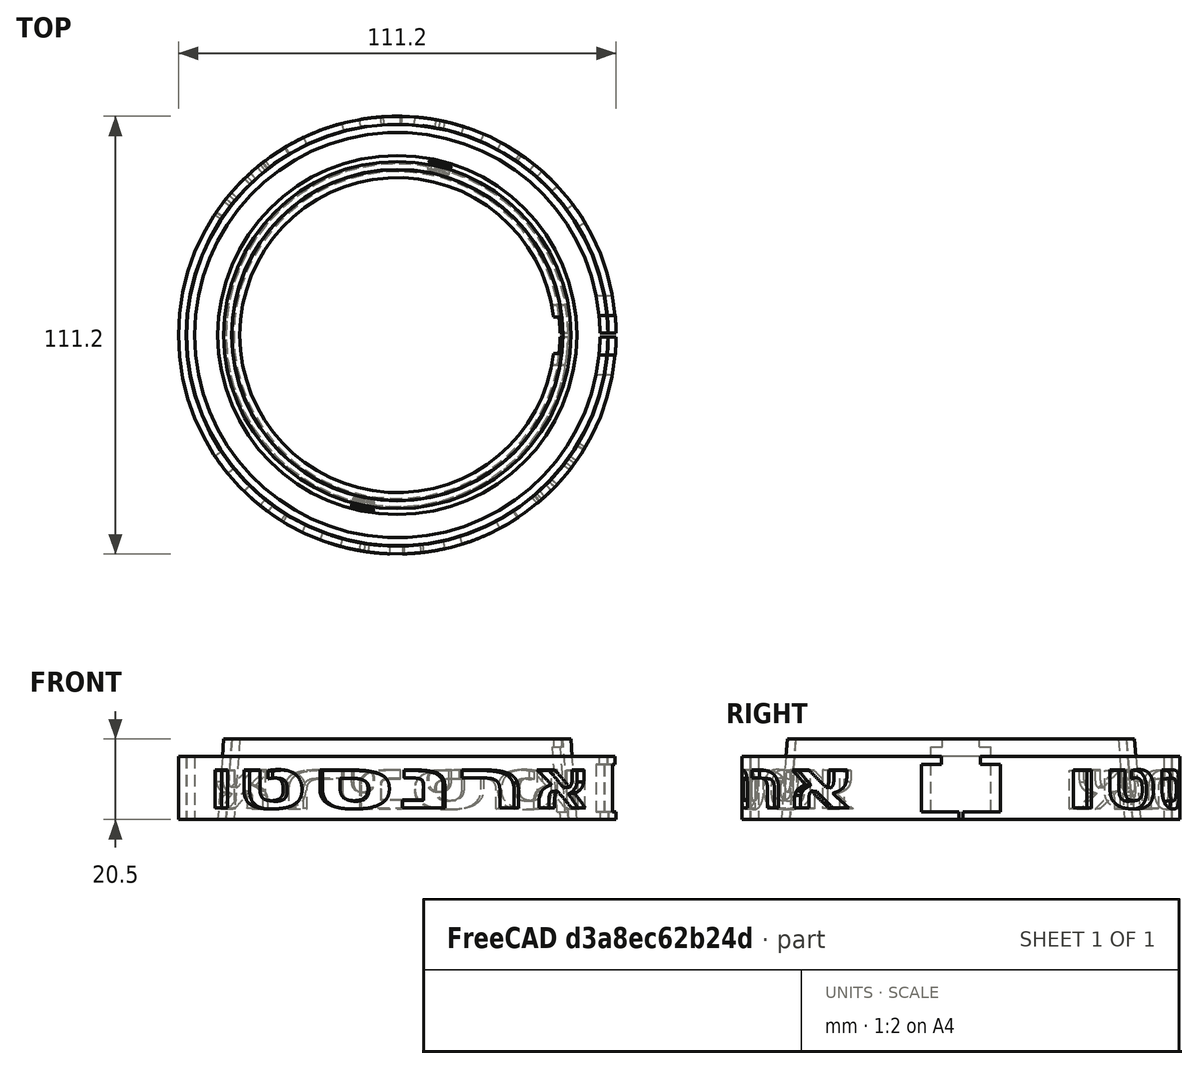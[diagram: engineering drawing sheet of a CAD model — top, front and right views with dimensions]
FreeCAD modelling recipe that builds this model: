
FCSTD DOCUMENT  (FreeCAD 0.20R29603 (Git))
Label: tazas
License: All rights reserved
LicenseURL: http://en.wikipedia.org/wiki/All_rights_reserved
objects: Part::Box×12, Part::Cut×11, Part::Feature×7, App::DocumentObjectGroup×7, Part::Cone×6, Sketcher::SketchObject×5, Part::Cylinder×4, Part::MultiFuse×4, Mesh::Feature×4, Part::FeaturePython×3
note: 52 computed .brp shape members not serialized (recipe doc carries the construction recipe); baked Part::Feature solids carry a one-line shape summary decoded from their .brp

FEATURE [Part::Cylinder] Cylinder  label="Cylinder_chico"
  Angle = 360
  AttacherType = Attacher::AttachEngine3D
  FirstAngle = 0
  Height = 16
  Radius = 51.5
  SecondAngle = 0
FEATURE [Part::Cylinder] Cylinder001  label="Cylinder00_grande"
  Angle = 360
  AttacherType = Attacher::AttachEngine3D
  FirstAngle = 0
  Height = 16
  Radius = 53.5
  SecondAngle = 0
FEATURE [Part::Cone] Cone  label="Cone_chico"
  Angle = 360
  AttacherType = Attacher::AttachEngine3D
  Height = 20.5
  Radius1 = 41.5
  Radius2 = 40
FEATURE [Part::Cone] Cone001  label="Cone001_grande"
  Angle = 360
  AttacherType = Attacher::AttachEngine3D
  Height = 20.5
  Radius1 = 43.5
  Radius2 = 42
FEATURE [Part::Box] Box  label="Cube"
  AttacherType = Attacher::AttachEngine3D
  Height = 12
  Length = 25
  Placement = pos=(40,-10,2) rot=(0,0,1;0rad)
  Width = 20
FEATURE [Part::Box] Box002  label="Cube002"
  AttacherType = Attacher::AttachEngine3D
  Height = 25.45
  Length = 25
  Placement = pos=(40,-5,2.55) rot=(0,0,1;0rad)
  Width = 10
FEATURE [Part::Box] Box003  label="Cube003"
  AttacherType = Attacher::AttachEngine3D
  Height = 12
  Length = 25
  Placement = pos=(40,-10,2) rot=(0,0,1;0rad)
  Width = 20
FEATURE [Part::Box] Box004  label="Cube004"
  AttacherType = Attacher::AttachEngine3D
  Height = 25.45
  Length = 25
  Placement = pos=(40,-5,4) rot=(0,0,1;0rad)
  Width = 10
FEATURE [Part::Cylinder] Cylinder002  label="Cylinder002_chico"
  Angle = 360
  AttacherType = Attacher::AttachEngine3D
  FirstAngle = 0
  Height = 16
  Radius = 53.6
  SecondAngle = 0
FEATURE [Part::Cylinder] Cylinder003  label="Cylinder003-grande"
  Angle = 360
  AttacherType = Attacher::AttachEngine3D
  FirstAngle = 0
  Height = 16
  Radius = 55.6
  SecondAngle = 0
FEATURE [Part::Box] Box006  label="Cube006"
  AttacherType = Attacher::AttachEngine3D
  Height = 16.5
  Length = 30
  Placement = pos=(24,-7.65,2) rot=(0,0,1;0rad)
  Width = 15.3
FEATURE [Part::Box] Box007  label="Cube007"
  AttacherType = Attacher::AttachEngine3D
  Height = 25.5
  Length = 30
  Placement = pos=(24,-4.65,2) rot=(0,0,1;0rad)
  Width = 9.3
FEATURE [Part::Cone] Cone002  label="Cone_chico001"
  Angle = 360
  AttacherType = Attacher::AttachEngine3D
  Height = 20.5
  Radius1 = 43.6
  Radius2 = 42.1
FEATURE [Part::Cone] Cone003  label="Cone001_grande001"
  Angle = 360
  AttacherType = Attacher::AttachEngine3D
  Height = 20.5
  Radius1 = 45.6
  Radius2 = 44.1
FEATURE [Part::Feature] Face003
  shape: bbox 14.35 x 9.888 x 2.467e-07 mm, 1 faces, 0 solids (baked)
FEATURE [Part::Feature] Face004
  shape: bbox 5.698 x 5.643 x 2.467e-07 mm, 1 faces, 0 solids (baked)
FEATURE [Part::Feature] Compound
  Placement = pos=(69.91,10.15,0) rot=(0,0,1;0rad)
  shape: bbox 89.01 x 10 x 2.467e-07 mm, 6 faces, 0 solids (baked)
FEATURE [Part::Feature] Compound001
  Placement = pos=(189.91,10.15,0) rot=(0,0,1;0rad)
  shape: bbox 89.01 x 10 x 2.467e-07 mm, 6 faces, 0 solids (baked)
FEATURE [Part::Feature] Compound004  label="2_ernesto"
  Placement = pos=(-33.35,18,0) rot=(1,0,0;0rad)
  shape: bbox 229.5 x 10 x 2.467e-07 mm, 12 faces, 0 solids (baked)
FEATURE [Part::Cut] Cut015014  label="taza_interior"
  Base = -> Cone001
  Tool = -> Cone
FEATURE [Part::Cut] Cut015018  label="cono"
  Base = -> Cone003
  Tool = -> Cone002
FEATURE [Part::Box] Box009  label="Cube009"
  AttacherType = Attacher::AttachEngine3D
  Height = 25.5
  Length = 30
  Placement = pos=(24,-0.5,-2) rot=(0,0,1;0rad)
  Width = 1
FEATURE [Part::Feature] Compound005  label="2_ernesto001"
  Placement = pos=(2.55,-16,0) rot=(1,0,0;3.14159rad)
  shape: bbox 229.5 x 10 x 2.467e-07 mm, 12 faces, 0 solids (baked)
FEATURE [Sketcher::SketchObject] Sketch  label="Sketch_con_2_ernesto"
  FullyConstrained = false
  sketch-geometry (180):
    g0: BSplineCurve PolesCount=2 KnotsCount=2 Degree=1 IsPeriodic=0
    g1: BSplineCurve PolesCount=3 KnotsCount=2 Degree=2 IsPeriodic=0
    g2: BSplineCurve PolesCount=3 KnotsCount=2 Degree=2 IsPeriodic=0
    g3: BSplineCurve PolesCount=3 KnotsCount=2 Degree=2 IsPeriodic=0
    g4: BSplineCurve PolesCount=3 KnotsCount=2 Degree=2 IsPeriodic=0
    g5: BSplineCurve PolesCount=3 KnotsCount=2 Degree=2 IsPeriodic=0
    g6: BSplineCurve PolesCount=3 KnotsCount=2 Degree=2 IsPeriodic=0
    g7: BSplineCurve PolesCount=2 KnotsCount=2 Degree=1 IsPeriodic=0
    g8: BSplineCurve PolesCount=3 KnotsCount=2 Degree=2 IsPeriodic=0
    g9: BSplineCurve PolesCount=2 KnotsCount=2 Degree=1 IsPeriodic=0
    g10: BSplineCurve PolesCount=2 KnotsCount=2 Degree=1 IsPeriodic=0
    g11: BSplineCurve PolesCount=3 KnotsCount=2 Degree=2 IsPeriodic=0
    g12: BSplineCurve PolesCount=3 KnotsCount=2 Degree=2 IsPeriodic=0
    g13: BSplineCurve PolesCount=3 KnotsCount=2 Degree=2 IsPeriodic=0
    g14: BSplineCurve PolesCount=3 KnotsCount=2 Degree=2 IsPeriodic=0
    g15: BSplineCurve PolesCount=3 KnotsCount=2 Degree=2 IsPeriodic=0
    g16: BSplineCurve PolesCount=2 KnotsCount=2 Degree=1 IsPeriodic=0
    g17: BSplineCurve PolesCount=2 KnotsCount=2 Degree=1 IsPeriodic=0
    g18: BSplineCurve PolesCount=2 KnotsCount=2 Degree=1 IsPeriodic=0
    g19: BSplineCurve PolesCount=3 KnotsCount=2 Degree=2 IsPeriodic=0
    g20: BSplineCurve PolesCount=2 KnotsCount=2 Degree=1 IsPeriodic=0
    g21: BSplineCurve PolesCount=2 KnotsCount=2 Degree=1 IsPeriodic=0
    g22: BSplineCurve PolesCount=2 KnotsCount=2 Degree=1 IsPeriodic=0
    g23: BSplineCurve PolesCount=3 KnotsCount=2 Degree=2 IsPeriodic=0
    g24: BSplineCurve PolesCount=3 KnotsCount=2 Degree=2 IsPeriodic=0
    g25: BSplineCurve PolesCount=3 KnotsCount=2 Degree=2 IsPeriodic=0
    g26: BSplineCurve PolesCount=3 KnotsCount=2 Degree=2 IsPeriodic=0
    g27: BSplineCurve PolesCount=3 KnotsCount=2 Degree=2 IsPeriodic=0
    g28: BSplineCurve PolesCount=2 KnotsCount=2 Degree=1 IsPeriodic=0
    g29: BSplineCurve PolesCount=2 KnotsCount=2 Degree=1 IsPeriodic=0
    g30: BSplineCurve PolesCount=2 KnotsCount=2 Degree=1 IsPeriodic=0
    g31: BSplineCurve PolesCount=3 KnotsCount=2 Degree=2 IsPeriodic=0
    g32: BSplineCurve PolesCount=2 KnotsCount=2 Degree=1 IsPeriodic=0
    g33: BSplineCurve PolesCount=2 KnotsCount=2 Degree=1 IsPeriodic=0
    g34: BSplineCurve PolesCount=2 KnotsCount=2 Degree=1 IsPeriodic=0
    g35: BSplineCurve PolesCount=3 KnotsCount=2 Degree=2 IsPeriodic=0
    g36: BSplineCurve PolesCount=3 KnotsCount=2 Degree=2 IsPeriodic=0
    g37: BSplineCurve PolesCount=3 KnotsCount=2 Degree=2 IsPeriodic=0
    g38: BSplineCurve PolesCount=3 KnotsCount=2 Degree=2 IsPeriodic=0
    g39: BSplineCurve PolesCount=3 KnotsCount=2 Degree=2 IsPeriodic=0
    g40: BSplineCurve PolesCount=3 KnotsCount=2 Degree=2 IsPeriodic=0
    g41: BSplineCurve PolesCount=3 KnotsCount=2 Degree=2 IsPeriodic=0
    g42: BSplineCurve PolesCount=2 KnotsCount=2 Degree=1 IsPeriodic=0
    g43: BSplineCurve PolesCount=2 KnotsCount=2 Degree=1 IsPeriodic=0
    g44: BSplineCurve PolesCount=2 KnotsCount=2 Degree=1 IsPeriodic=0
    g45: BSplineCurve PolesCount=2 KnotsCount=2 Degree=1 IsPeriodic=0
    g46: BSplineCurve PolesCount=3 KnotsCount=2 Degree=2 IsPeriodic=0
    g47: BSplineCurve PolesCount=3 KnotsCount=2 Degree=2 IsPeriodic=0
    g48: BSplineCurve PolesCount=2 KnotsCount=2 Degree=1 IsPeriodic=0
    g49: BSplineCurve PolesCount=2 KnotsCount=2 Degree=1 IsPeriodic=0
    g50: BSplineCurve PolesCount=2 KnotsCount=2 Degree=1 IsPeriodic=0
    g51: BSplineCurve PolesCount=3 KnotsCount=2 Degree=2 IsPeriodic=0
    g52: BSplineCurve PolesCount=3 KnotsCount=2 Degree=2 IsPeriodic=0
    g53: BSplineCurve PolesCount=3 KnotsCount=2 Degree=2 IsPeriodic=0
    g54: BSplineCurve PolesCount=3 KnotsCount=2 Degree=2 IsPeriodic=0
    g55: BSplineCurve PolesCount=3 KnotsCount=2 Degree=2 IsPeriodic=0
    g56: BSplineCurve PolesCount=2 KnotsCount=2 Degree=1 IsPeriodic=0
    g57: BSplineCurve PolesCount=3 KnotsCount=2 Degree=2 IsPeriodic=0
    g58: BSplineCurve PolesCount=3 KnotsCount=2 Degree=2 IsPeriodic=0
    g59: BSplineCurve PolesCount=2 KnotsCount=2 Degree=1 IsPeriodic=0
    g60: BSplineCurve PolesCount=2 KnotsCount=2 Degree=1 IsPeriodic=0
    g61: BSplineCurve PolesCount=2 KnotsCount=2 Degree=1 IsPeriodic=0
    g62: BSplineCurve PolesCount=3 KnotsCount=2 Degree=2 IsPeriodic=0
    g63: BSplineCurve PolesCount=3 KnotsCount=2 Degree=2 IsPeriodic=0
    g64: BSplineCurve PolesCount=2 KnotsCount=2 Degree=1 IsPeriodic=0
    g65: BSplineCurve PolesCount=2 KnotsCount=2 Degree=1 IsPeriodic=0
    g66: BSplineCurve PolesCount=2 KnotsCount=2 Degree=1 IsPeriodic=0
    g67: BSplineCurve PolesCount=2 KnotsCount=2 Degree=1 IsPeriodic=0
    g68: BSplineCurve PolesCount=2 KnotsCount=2 Degree=1 IsPeriodic=0
    g69: BSplineCurve PolesCount=3 KnotsCount=2 Degree=2 IsPeriodic=0
    g70: BSplineCurve PolesCount=3 KnotsCount=2 Degree=2 IsPeriodic=0
    g71: BSplineCurve PolesCount=3 KnotsCount=2 Degree=2 IsPeriodic=0
    g72: BSplineCurve PolesCount=3 KnotsCount=2 Degree=2 IsPeriodic=0
    g73: BSplineCurve PolesCount=3 KnotsCount=2 Degree=2 IsPeriodic=0
    g74: BSplineCurve PolesCount=3 KnotsCount=2 Degree=2 IsPeriodic=0
    g75: BSplineCurve PolesCount=3 KnotsCount=2 Degree=2 IsPeriodic=0
    g76: BSplineCurve PolesCount=2 KnotsCount=2 Degree=1 IsPeriodic=0
    g77: BSplineCurve PolesCount=3 KnotsCount=2 Degree=2 IsPeriodic=0
    g78: BSplineCurve PolesCount=3 KnotsCount=2 Degree=2 IsPeriodic=0
    g79: BSplineCurve PolesCount=3 KnotsCount=2 Degree=2 IsPeriodic=0
    g80: BSplineCurve PolesCount=3 KnotsCount=2 Degree=2 IsPeriodic=0
    g81: BSplineCurve PolesCount=3 KnotsCount=2 Degree=2 IsPeriodic=0
    g82: BSplineCurve PolesCount=3 KnotsCount=2 Degree=2 IsPeriodic=0
    g83: BSplineCurve PolesCount=3 KnotsCount=2 Degree=2 IsPeriodic=0
    g84: BSplineCurve PolesCount=2 KnotsCount=2 Degree=1 IsPeriodic=0
    g85: BSplineCurve PolesCount=2 KnotsCount=2 Degree=1 IsPeriodic=0
    g86: BSplineCurve PolesCount=2 KnotsCount=2 Degree=1 IsPeriodic=0
    g87: BSplineCurve PolesCount=2 KnotsCount=2 Degree=1 IsPeriodic=0
    g88: BSplineCurve PolesCount=2 KnotsCount=2 Degree=1 IsPeriodic=0
    g89: BSplineCurve PolesCount=2 KnotsCount=2 Degree=1 IsPeriodic=0
    g90: BSplineCurve PolesCount=2 KnotsCount=2 Degree=1 IsPeriodic=0
    g91: BSplineCurve PolesCount=3 KnotsCount=2 Degree=2 IsPeriodic=0
    g92: BSplineCurve PolesCount=3 KnotsCount=2 Degree=2 IsPeriodic=0
    g93: BSplineCurve PolesCount=3 KnotsCount=2 Degree=2 IsPeriodic=0
    g94: BSplineCurve PolesCount=3 KnotsCount=2 Degree=2 IsPeriodic=0
    g95: BSplineCurve PolesCount=3 KnotsCount=2 Degree=2 IsPeriodic=0
    g96: BSplineCurve PolesCount=3 KnotsCount=2 Degree=2 IsPeriodic=0
    g97: BSplineCurve PolesCount=2 KnotsCount=2 Degree=1 IsPeriodic=0
    g98: BSplineCurve PolesCount=3 KnotsCount=2 Degree=2 IsPeriodic=0
    g99: BSplineCurve PolesCount=2 KnotsCount=2 Degree=1 IsPeriodic=0
    g100: BSplineCurve PolesCount=2 KnotsCount=2 Degree=1 IsPeriodic=0
    g101: BSplineCurve PolesCount=3 KnotsCount=2 Degree=2 IsPeriodic=0
    g102: BSplineCurve PolesCount=3 KnotsCount=2 Degree=2 IsPeriodic=0
    g103: BSplineCurve PolesCount=3 KnotsCount=2 Degree=2 IsPeriodic=0
    g104: BSplineCurve PolesCount=3 KnotsCount=2 Degree=2 IsPeriodic=0
    g105: BSplineCurve PolesCount=3 KnotsCount=2 Degree=2 IsPeriodic=0
    g106: BSplineCurve PolesCount=2 KnotsCount=2 Degree=1 IsPeriodic=0
    g107: BSplineCurve PolesCount=2 KnotsCount=2 Degree=1 IsPeriodic=0
    g108: BSplineCurve PolesCount=2 KnotsCount=2 Degree=1 IsPeriodic=0
    g109: BSplineCurve PolesCount=3 KnotsCount=2 Degree=2 IsPeriodic=0
    g110: BSplineCurve PolesCount=2 KnotsCount=2 Degree=1 IsPeriodic=0
    g111: BSplineCurve PolesCount=2 KnotsCount=2 Degree=1 IsPeriodic=0
    g112: BSplineCurve PolesCount=2 KnotsCount=2 Degree=1 IsPeriodic=0
    g113: BSplineCurve PolesCount=3 KnotsCount=2 Degree=2 IsPeriodic=0
    g114: BSplineCurve PolesCount=3 KnotsCount=2 Degree=2 IsPeriodic=0
    g115: BSplineCurve PolesCount=3 KnotsCount=2 Degree=2 IsPeriodic=0
    g116: BSplineCurve PolesCount=3 KnotsCount=2 Degree=2 IsPeriodic=0
    g117: BSplineCurve PolesCount=3 KnotsCount=2 Degree=2 IsPeriodic=0
    g118: BSplineCurve PolesCount=2 KnotsCount=2 Degree=1 IsPeriodic=0
    g119: BSplineCurve PolesCount=2 KnotsCount=2 Degree=1 IsPeriodic=0
    g120: BSplineCurve PolesCount=2 KnotsCount=2 Degree=1 IsPeriodic=0
    g121: BSplineCurve PolesCount=3 KnotsCount=2 Degree=2 IsPeriodic=0
    g122: BSplineCurve PolesCount=2 KnotsCount=2 Degree=1 IsPeriodic=0
    g123: BSplineCurve PolesCount=2 KnotsCount=2 Degree=1 IsPeriodic=0
    g124: BSplineCurve PolesCount=2 KnotsCount=2 Degree=1 IsPeriodic=0
    g125: BSplineCurve PolesCount=3 KnotsCount=2 Degree=2 IsPeriodic=0
    g126: BSplineCurve PolesCount=3 KnotsCount=2 Degree=2 IsPeriodic=0
    g127: BSplineCurve PolesCount=3 KnotsCount=2 Degree=2 IsPeriodic=0
    g128: BSplineCurve PolesCount=3 KnotsCount=2 Degree=2 IsPeriodic=0
    g129: BSplineCurve PolesCount=3 KnotsCount=2 Degree=2 IsPeriodic=0
    g130: BSplineCurve PolesCount=3 KnotsCount=2 Degree=2 IsPeriodic=0
    g131: BSplineCurve PolesCount=3 KnotsCount=2 Degree=2 IsPeriodic=0
    g132: BSplineCurve PolesCount=2 KnotsCount=2 Degree=1 IsPeriodic=0
    g133: BSplineCurve PolesCount=2 KnotsCount=2 Degree=1 IsPeriodic=0
    g134: BSplineCurve PolesCount=2 KnotsCount=2 Degree=1 IsPeriodic=0
    g135: BSplineCurve PolesCount=2 KnotsCount=2 Degree=1 IsPeriodic=0
    g136: BSplineCurve PolesCount=3 KnotsCount=2 Degree=2 IsPeriodic=0
    g137: BSplineCurve PolesCount=3 KnotsCount=2 Degree=2 IsPeriodic=0
    g138: BSplineCurve PolesCount=2 KnotsCount=2 Degree=1 IsPeriodic=0
    g139: BSplineCurve PolesCount=2 KnotsCount=2 Degree=1 IsPeriodic=0
    g140: BSplineCurve PolesCount=2 KnotsCount=2 Degree=1 IsPeriodic=0
    g141: BSplineCurve PolesCount=3 KnotsCount=2 Degree=2 IsPeriodic=0
    g142: BSplineCurve PolesCount=3 KnotsCount=2 Degree=2 IsPeriodic=0
    g143: BSplineCurve PolesCount=3 KnotsCount=2 Degree=2 IsPeriodic=0
    g144: BSplineCurve PolesCount=3 KnotsCount=2 Degree=2 IsPeriodic=0
    g145: BSplineCurve PolesCount=3 KnotsCount=2 Degree=2 IsPeriodic=0
    g146: BSplineCurve PolesCount=2 KnotsCount=2 Degree=1 IsPeriodic=0
    g147: BSplineCurve PolesCount=3 KnotsCount=2 Degree=2 IsPeriodic=0
    g148: BSplineCurve PolesCount=3 KnotsCount=2 Degree=2 IsPeriodic=0
    g149: BSplineCurve PolesCount=2 KnotsCount=2 Degree=1 IsPeriodic=0
    g150: BSplineCurve PolesCount=2 KnotsCount=2 Degree=1 IsPeriodic=0
    g151: BSplineCurve PolesCount=2 KnotsCount=2 Degree=1 IsPeriodic=0
    g152: BSplineCurve PolesCount=3 KnotsCount=2 Degree=2 IsPeriodic=0
    g153: BSplineCurve PolesCount=3 KnotsCount=2 Degree=2 IsPeriodic=0
    g154: BSplineCurve PolesCount=2 KnotsCount=2 Degree=1 IsPeriodic=0
    g155: BSplineCurve PolesCount=2 KnotsCount=2 Degree=1 IsPeriodic=0
    g156: BSplineCurve PolesCount=2 KnotsCount=2 Degree=1 IsPeriodic=0
    g157: BSplineCurve PolesCount=2 KnotsCount=2 Degree=1 IsPeriodic=0
    g158: BSplineCurve PolesCount=2 KnotsCount=2 Degree=1 IsPeriodic=0
    g159: BSplineCurve PolesCount=3 KnotsCount=2 Degree=2 IsPeriodic=0
    g160: BSplineCurve PolesCount=3 KnotsCount=2 Degree=2 IsPeriodic=0
    g161: BSplineCurve PolesCount=3 KnotsCount=2 Degree=2 IsPeriodic=0
    g162: BSplineCurve PolesCount=3 KnotsCount=2 Degree=2 IsPeriodic=0
    g163: BSplineCurve PolesCount=3 KnotsCount=2 Degree=2 IsPeriodic=0
    g164: BSplineCurve PolesCount=3 KnotsCount=2 Degree=2 IsPeriodic=0
    g165: BSplineCurve PolesCount=3 KnotsCount=2 Degree=2 IsPeriodic=0
    g166: BSplineCurve PolesCount=2 KnotsCount=2 Degree=1 IsPeriodic=0
    g167: BSplineCurve PolesCount=3 KnotsCount=2 Degree=2 IsPeriodic=0
    g168: BSplineCurve PolesCount=3 KnotsCount=2 Degree=2 IsPeriodic=0
    g169: BSplineCurve PolesCount=3 KnotsCount=2 Degree=2 IsPeriodic=0
    g170: BSplineCurve PolesCount=3 KnotsCount=2 Degree=2 IsPeriodic=0
    g171: BSplineCurve PolesCount=3 KnotsCount=2 Degree=2 IsPeriodic=0
    g172: BSplineCurve PolesCount=3 KnotsCount=2 Degree=2 IsPeriodic=0
    g173: BSplineCurve PolesCount=3 KnotsCount=2 Degree=2 IsPeriodic=0
    g174: BSplineCurve PolesCount=2 KnotsCount=2 Degree=1 IsPeriodic=0
    g175: BSplineCurve PolesCount=2 KnotsCount=2 Degree=1 IsPeriodic=0
    g176: BSplineCurve PolesCount=2 KnotsCount=2 Degree=1 IsPeriodic=0
    g177: BSplineCurve PolesCount=2 KnotsCount=2 Degree=1 IsPeriodic=0
    g178: BSplineCurve PolesCount=2 KnotsCount=2 Degree=1 IsPeriodic=0
    g179: BSplineCurve PolesCount=2 KnotsCount=2 Degree=1 IsPeriodic=0
  constraints (180):
    c: Coincident(g0,g1)
    c: Coincident(g1,g2)
    c: Coincident(g2,g3)
    c: Coincident(g3,g4)
    c: Coincident(g4,g5)
    c: Coincident(g5,g6)
    c: Coincident(g6,g7)
    c: Coincident(g7,g0)
    c: Coincident(g8,g9)
    c: Coincident(g9,g10)
    c: Coincident(g10,g11)
    c: Coincident(g11,g12)
    c: Coincident(g12,g13)
    c: Coincident(g13,g14)
    c: Coincident(g14,g15)
    c: Coincident(g15,g8)
    c: Coincident(g16,g17)
    c: Coincident(g17,g18)
    c: Coincident(g18,g19)
    c: Coincident(g19,g20)
    c: Coincident(g20,g21)
    c: Coincident(g21,g22)
    c: Coincident(g22,g23)
    c: Coincident(g23,g24)
    c: Coincident(g24,g25)
    c: Coincident(g25,g26)
    c: Coincident(g26,g27)
    c: Coincident(g27,g28)
    c: Coincident(g28,g29)
    c: Coincident(g29,g30)
    c: Coincident(g30,g31)
    c: Coincident(g31,g32)
    c: Coincident(g32,g33)
    c: Coincident(g33,g34)
    c: Coincident(g34,g35)
    c: Coincident(g35,g36)
    c: Coincident(g36,g37)
    c: Coincident(g37,g38)
    c: Coincident(g38,g39)
    c: Coincident(g39,g40)
    c: Coincident(g40,g41)
    c: Coincident(g41,g42)
    c: Coincident(g42,g16)
    c: Coincident(g43,g44)
    c: Coincident(g44,g45)
    c: Coincident(g45,g46)
    c: Coincident(g46,g47)
    c: Coincident(g47,g48)
    c: Coincident(g48,g49)
    c: Coincident(g49,g50)
    c: Coincident(g50,g51)
    c: Coincident(g51,g52)
    c: Coincident(g52,g53)
    c: Coincident(g53,g54)
    c: Coincident(g54,g55)
    c: Coincident(g55,g43)
    c: Coincident(g56,g57)
    c: Coincident(g57,g58)
    c: Coincident(g58,g59)
    c: Coincident(g59,g60)
    c: Coincident(g60,g61)
    c: Coincident(g61,g62)
    c: Coincident(g62,g63)
    c: Coincident(g63,g64)
    c: Coincident(g64,g65)
    c: Coincident(g65,g66)
    c: Coincident(g66,g67)
    c: Coincident(g67,g56)
    c: Coincident(g68,g69)
    c: Coincident(g69,g70)
    c: Coincident(g70,g71)
    c: Coincident(g71,g72)
    c: Coincident(g72,g73)
    c: Coincident(g73,g74)
    c: Coincident(g74,g75)
    c: Coincident(g75,g76)
    c: Coincident(g76,g77)
    c: Coincident(g77,g78)
    c: Coincident(g78,g79)
    c: Coincident(g79,g80)
    c: Coincident(g80,g81)
    c: Coincident(g81,g82)
    c: Coincident(g82,g83)
    c: Coincident(g83,g84)
    c: Coincident(g84,g85)
    c: Coincident(g85,g68)
    c: Coincident(g86,g87)
    c: Coincident(g87,g88)
    c: Coincident(g88,g89)
    c: Coincident(g89,g86)
    c: Coincident(g90,g91)
    c: Coincident(g91,g92)
    c: Coincident(g92,g93)
    c: Coincident(g93,g94)
    c: Coincident(g94,g95)
    c: Coincident(g95,g96)
    c: Coincident(g96,g97)
    c: Coincident(g97,g90)
    c: Coincident(g98,g99)
    c: Coincident(g99,g100)
    c: Coincident(g100,g101)
    c: Coincident(g101,g102)
    c: Coincident(g102,g103)
    c: Coincident(g103,g104)
    c: Coincident(g104,g105)
    c: Coincident(g105,g98)
    c: Coincident(g106,g107)
    c: Coincident(g107,g108)
    c: Coincident(g108,g109)
    c: Coincident(g109,g110)
    c: Coincident(g110,g111)
    c: Coincident(g111,g112)
    c: Coincident(g112,g113)
    c: Coincident(g113,g114)
    c: Coincident(g114,g115)
    c: Coincident(g115,g116)
    c: Coincident(g116,g117)
    c: Coincident(g117,g118)
    c: Coincident(g118,g119)
    c: Coincident(g119,g120)
    c: Coincident(g120,g121)
    c: Coincident(g121,g122)
    c: Coincident(g122,g123)
    c: Coincident(g123,g124)
    c: Coincident(g124,g125)
    c: Coincident(g125,g126)
    c: Coincident(g126,g127)
    c: Coincident(g127,g128)
    c: Coincident(g128,g129)
    c: Coincident(g129,g130)
    c: Coincident(g130,g131)
    c: Coincident(g131,g132)
    c: Coincident(g132,g106)
    c: Coincident(g133,g134)
    c: Coincident(g134,g135)
    c: Coincident(g135,g136)
    c: Coincident(g136,g137)
    c: Coincident(g137,g138)
    c: Coincident(g138,g139)
    c: Coincident(g139,g140)
    c: Coincident(g140,g141)
    c: Coincident(g141,g142)
    c: Coincident(g142,g143)
    c: Coincident(g143,g144)
    c: Coincident(g144,g145)
    c: Coincident(g145,g133)
    c: Coincident(g146,g147)
    c: Coincident(g147,g148)
    c: Coincident(g148,g149)
    c: Coincident(g149,g150)
    c: Coincident(g150,g151)
    c: Coincident(g151,g152)
    c: Coincident(g152,g153)
    c: Coincident(g153,g154)
    c: Coincident(g154,g155)
    c: Coincident(g155,g156)
    c: Coincident(g156,g157)
    c: Coincident(g157,g146)
    c: Coincident(g158,g159)
    c: Coincident(g159,g160)
    c: Coincident(g160,g161)
    c: Coincident(g161,g162)
    c: Coincident(g162,g163)
    c: Coincident(g163,g164)
    c: Coincident(g164,g165)
    c: Coincident(g165,g166)
    c: Coincident(g166,g167)
    c: Coincident(g167,g168)
    c: Coincident(g168,g169)
    c: Coincident(g169,g170)
    c: Coincident(g170,g171)
    c: Coincident(g171,g172)
    c: Coincident(g172,g173)
    c: Coincident(g173,g174)
    c: Coincident(g174,g175)
    c: Coincident(g175,g158)
    c: Coincident(g176,g177)
    c: Coincident(g177,g178)
    c: Coincident(g178,g179)
    c: Coincident(g179,g176)
FEATURE [Sketcher::SketchObject] Mapped_Sketch
  FullyConstrained = false
  Support = -> [Cut015018]
  sketch-geometry (184):
    g0: LineSegment StartX=0 StartY=0 StartZ=0 EndX=277 EndY=0 EndZ=0
    g1: LineSegment StartX=277 StartY=0 StartZ=0 EndX=277 EndY=20.5548 EndZ=0
    g2: LineSegment StartX=277 StartY=20.5548 StartZ=0 EndX=0 EndY=20.5548 EndZ=0
    g3: LineSegment StartX=0 StartY=20.5548 StartZ=0 EndX=0 EndY=0 EndZ=0
    g4: BSplineCurve PolesCount=2 KnotsCount=2 Degree=1 IsPeriodic=0
    g5: BSplineCurve PolesCount=3 KnotsCount=2 Degree=2 IsPeriodic=0
    g6: BSplineCurve PolesCount=3 KnotsCount=2 Degree=2 IsPeriodic=0
    g7: BSplineCurve PolesCount=3 KnotsCount=2 Degree=2 IsPeriodic=0
    g8: BSplineCurve PolesCount=3 KnotsCount=2 Degree=2 IsPeriodic=0
    g9: BSplineCurve PolesCount=3 KnotsCount=2 Degree=2 IsPeriodic=0
    g10: BSplineCurve PolesCount=3 KnotsCount=2 Degree=2 IsPeriodic=0
    g11: BSplineCurve PolesCount=2 KnotsCount=2 Degree=1 IsPeriodic=0
    g12: BSplineCurve PolesCount=3 KnotsCount=2 Degree=2 IsPeriodic=0
    g13: BSplineCurve PolesCount=2 KnotsCount=2 Degree=1 IsPeriodic=0
    g14: BSplineCurve PolesCount=2 KnotsCount=2 Degree=1 IsPeriodic=0
    g15: BSplineCurve PolesCount=3 KnotsCount=2 Degree=2 IsPeriodic=0
    g16: BSplineCurve PolesCount=3 KnotsCount=2 Degree=2 IsPeriodic=0
    g17: BSplineCurve PolesCount=3 KnotsCount=2 Degree=2 IsPeriodic=0
    g18: BSplineCurve PolesCount=3 KnotsCount=2 Degree=2 IsPeriodic=0
    g19: BSplineCurve PolesCount=3 KnotsCount=2 Degree=2 IsPeriodic=0
    g20: BSplineCurve PolesCount=2 KnotsCount=2 Degree=1 IsPeriodic=0
    g21: BSplineCurve PolesCount=2 KnotsCount=2 Degree=1 IsPeriodic=0
    g22: BSplineCurve PolesCount=2 KnotsCount=2 Degree=1 IsPeriodic=0
    g23: BSplineCurve PolesCount=3 KnotsCount=2 Degree=2 IsPeriodic=0
    g24: BSplineCurve PolesCount=2 KnotsCount=2 Degree=1 IsPeriodic=0
    g25: BSplineCurve PolesCount=2 KnotsCount=2 Degree=1 IsPeriodic=0
    g26: BSplineCurve PolesCount=2 KnotsCount=2 Degree=1 IsPeriodic=0
    g27: BSplineCurve PolesCount=3 KnotsCount=2 Degree=2 IsPeriodic=0
    g28: BSplineCurve PolesCount=3 KnotsCount=2 Degree=2 IsPeriodic=0
    g29: BSplineCurve PolesCount=3 KnotsCount=2 Degree=2 IsPeriodic=0
    g30: BSplineCurve PolesCount=3 KnotsCount=2 Degree=2 IsPeriodic=0
    g31: BSplineCurve PolesCount=3 KnotsCount=2 Degree=2 IsPeriodic=0
    g32: BSplineCurve PolesCount=2 KnotsCount=2 Degree=1 IsPeriodic=0
    g33: BSplineCurve PolesCount=2 KnotsCount=2 Degree=1 IsPeriodic=0
    g34: BSplineCurve PolesCount=2 KnotsCount=2 Degree=1 IsPeriodic=0
    g35: BSplineCurve PolesCount=3 KnotsCount=2 Degree=2 IsPeriodic=0
    g36: BSplineCurve PolesCount=2 KnotsCount=2 Degree=1 IsPeriodic=0
    g37: BSplineCurve PolesCount=2 KnotsCount=2 Degree=1 IsPeriodic=0
    g38: BSplineCurve PolesCount=2 KnotsCount=2 Degree=1 IsPeriodic=0
    g39: BSplineCurve PolesCount=3 KnotsCount=2 Degree=2 IsPeriodic=0
    g40: BSplineCurve PolesCount=3 KnotsCount=2 Degree=2 IsPeriodic=0
    g41: BSplineCurve PolesCount=3 KnotsCount=2 Degree=2 IsPeriodic=0
    g42: BSplineCurve PolesCount=3 KnotsCount=2 Degree=2 IsPeriodic=0
    g43: BSplineCurve PolesCount=3 KnotsCount=2 Degree=2 IsPeriodic=0
    g44: BSplineCurve PolesCount=3 KnotsCount=2 Degree=2 IsPeriodic=0
    g45: BSplineCurve PolesCount=3 KnotsCount=2 Degree=2 IsPeriodic=0
    g46: BSplineCurve PolesCount=2 KnotsCount=2 Degree=1 IsPeriodic=0
    g47: BSplineCurve PolesCount=2 KnotsCount=2 Degree=1 IsPeriodic=0
    g48: BSplineCurve PolesCount=2 KnotsCount=2 Degree=1 IsPeriodic=0
    g49: BSplineCurve PolesCount=2 KnotsCount=2 Degree=1 IsPeriodic=0
    g50: BSplineCurve PolesCount=3 KnotsCount=2 Degree=2 IsPeriodic=0
    g51: BSplineCurve PolesCount=3 KnotsCount=2 Degree=2 IsPeriodic=0
    g52: BSplineCurve PolesCount=2 KnotsCount=2 Degree=1 IsPeriodic=0
    g53: BSplineCurve PolesCount=2 KnotsCount=2 Degree=1 IsPeriodic=0
    g54: BSplineCurve PolesCount=2 KnotsCount=2 Degree=1 IsPeriodic=0
    g55: BSplineCurve PolesCount=3 KnotsCount=2 Degree=2 IsPeriodic=0
    g56: BSplineCurve PolesCount=3 KnotsCount=2 Degree=2 IsPeriodic=0
    g57: BSplineCurve PolesCount=3 KnotsCount=2 Degree=2 IsPeriodic=0
    g58: BSplineCurve PolesCount=3 KnotsCount=2 Degree=2 IsPeriodic=0
    g59: BSplineCurve PolesCount=3 KnotsCount=2 Degree=2 IsPeriodic=0
    g60: BSplineCurve PolesCount=2 KnotsCount=2 Degree=1 IsPeriodic=0
    g61: BSplineCurve PolesCount=3 KnotsCount=2 Degree=2 IsPeriodic=0
    g62: BSplineCurve PolesCount=3 KnotsCount=2 Degree=2 IsPeriodic=0
    g63: BSplineCurve PolesCount=2 KnotsCount=2 Degree=1 IsPeriodic=0
    g64: BSplineCurve PolesCount=2 KnotsCount=2 Degree=1 IsPeriodic=0
    g65: BSplineCurve PolesCount=2 KnotsCount=2 Degree=1 IsPeriodic=0
    g66: BSplineCurve PolesCount=3 KnotsCount=2 Degree=2 IsPeriodic=0
    g67: BSplineCurve PolesCount=3 KnotsCount=2 Degree=2 IsPeriodic=0
    g68: BSplineCurve PolesCount=2 KnotsCount=2 Degree=1 IsPeriodic=0
    g69: BSplineCurve PolesCount=2 KnotsCount=2 Degree=1 IsPeriodic=0
    g70: BSplineCurve PolesCount=2 KnotsCount=2 Degree=1 IsPeriodic=0
    g71: BSplineCurve PolesCount=2 KnotsCount=2 Degree=1 IsPeriodic=0
    g72: BSplineCurve PolesCount=2 KnotsCount=2 Degree=1 IsPeriodic=0
    g73: BSplineCurve PolesCount=3 KnotsCount=2 Degree=2 IsPeriodic=0
    g74: BSplineCurve PolesCount=3 KnotsCount=2 Degree=2 IsPeriodic=0
    g75: BSplineCurve PolesCount=3 KnotsCount=2 Degree=2 IsPeriodic=0
    g76: BSplineCurve PolesCount=3 KnotsCount=2 Degree=2 IsPeriodic=0
    g77: BSplineCurve PolesCount=3 KnotsCount=2 Degree=2 IsPeriodic=0
    g78: BSplineCurve PolesCount=3 KnotsCount=2 Degree=2 IsPeriodic=0
    g79: BSplineCurve PolesCount=3 KnotsCount=2 Degree=2 IsPeriodic=0
    g80: BSplineCurve PolesCount=2 KnotsCount=2 Degree=1 IsPeriodic=0
    g81: BSplineCurve PolesCount=3 KnotsCount=2 Degree=2 IsPeriodic=0
    g82: BSplineCurve PolesCount=3 KnotsCount=2 Degree=2 IsPeriodic=0
    g83: BSplineCurve PolesCount=3 KnotsCount=2 Degree=2 IsPeriodic=0
    g84: BSplineCurve PolesCount=3 KnotsCount=2 Degree=2 IsPeriodic=0
    g85: BSplineCurve PolesCount=3 KnotsCount=2 Degree=2 IsPeriodic=0
    g86: BSplineCurve PolesCount=3 KnotsCount=2 Degree=2 IsPeriodic=0
    g87: BSplineCurve PolesCount=3 KnotsCount=2 Degree=2 IsPeriodic=0
    g88: BSplineCurve PolesCount=2 KnotsCount=2 Degree=1 IsPeriodic=0
    g89: BSplineCurve PolesCount=2 KnotsCount=2 Degree=1 IsPeriodic=0
    g90: BSplineCurve PolesCount=2 KnotsCount=2 Degree=1 IsPeriodic=0
    g91: BSplineCurve PolesCount=2 KnotsCount=2 Degree=1 IsPeriodic=0
    g92: BSplineCurve PolesCount=2 KnotsCount=2 Degree=1 IsPeriodic=0
    g93: BSplineCurve PolesCount=2 KnotsCount=2 Degree=1 IsPeriodic=0
    g94: BSplineCurve PolesCount=2 KnotsCount=2 Degree=1 IsPeriodic=0
    g95: BSplineCurve PolesCount=3 KnotsCount=2 Degree=2 IsPeriodic=0
    g96: BSplineCurve PolesCount=3 KnotsCount=2 Degree=2 IsPeriodic=0
    g97: BSplineCurve PolesCount=3 KnotsCount=2 Degree=2 IsPeriodic=0
    g98: BSplineCurve PolesCount=3 KnotsCount=2 Degree=2 IsPeriodic=0
    g99: BSplineCurve PolesCount=3 KnotsCount=2 Degree=2 IsPeriodic=0
    g100: BSplineCurve PolesCount=3 KnotsCount=2 Degree=2 IsPeriodic=0
    g101: BSplineCurve PolesCount=2 KnotsCount=2 Degree=1 IsPeriodic=0
    g102: BSplineCurve PolesCount=3 KnotsCount=2 Degree=2 IsPeriodic=0
    g103: BSplineCurve PolesCount=2 KnotsCount=2 Degree=1 IsPeriodic=0
    g104: BSplineCurve PolesCount=2 KnotsCount=2 Degree=1 IsPeriodic=0
    g105: BSplineCurve PolesCount=3 KnotsCount=2 Degree=2 IsPeriodic=0
    g106: BSplineCurve PolesCount=3 KnotsCount=2 Degree=2 IsPeriodic=0
    g107: BSplineCurve PolesCount=3 KnotsCount=2 Degree=2 IsPeriodic=0
    g108: BSplineCurve PolesCount=3 KnotsCount=2 Degree=2 IsPeriodic=0
    g109: BSplineCurve PolesCount=3 KnotsCount=2 Degree=2 IsPeriodic=0
    g110: BSplineCurve PolesCount=2 KnotsCount=2 Degree=1 IsPeriodic=0
    g111: BSplineCurve PolesCount=2 KnotsCount=2 Degree=1 IsPeriodic=0
    g112: BSplineCurve PolesCount=2 KnotsCount=2 Degree=1 IsPeriodic=0
    g113: BSplineCurve PolesCount=3 KnotsCount=2 Degree=2 IsPeriodic=0
    g114: BSplineCurve PolesCount=2 KnotsCount=2 Degree=1 IsPeriodic=0
    g115: BSplineCurve PolesCount=2 KnotsCount=2 Degree=1 IsPeriodic=0
    g116: BSplineCurve PolesCount=2 KnotsCount=2 Degree=1 IsPeriodic=0
    g117: BSplineCurve PolesCount=3 KnotsCount=2 Degree=2 IsPeriodic=0
    g118: BSplineCurve PolesCount=3 KnotsCount=2 Degree=2 IsPeriodic=0
    g119: BSplineCurve PolesCount=3 KnotsCount=2 Degree=2 IsPeriodic=0
    g120: BSplineCurve PolesCount=3 KnotsCount=2 Degree=2 IsPeriodic=0
    g121: BSplineCurve PolesCount=3 KnotsCount=2 Degree=2 IsPeriodic=0
    g122: BSplineCurve PolesCount=2 KnotsCount=2 Degree=1 IsPeriodic=0
    g123: BSplineCurve PolesCount=2 KnotsCount=2 Degree=1 IsPeriodic=0
    g124: BSplineCurve PolesCount=2 KnotsCount=2 Degree=1 IsPeriodic=0
    g125: BSplineCurve PolesCount=3 KnotsCount=2 Degree=2 IsPeriodic=0
    g126: BSplineCurve PolesCount=2 KnotsCount=2 Degree=1 IsPeriodic=0
    g127: BSplineCurve PolesCount=2 KnotsCount=2 Degree=1 IsPeriodic=0
    g128: BSplineCurve PolesCount=2 KnotsCount=2 Degree=1 IsPeriodic=0
    g129: BSplineCurve PolesCount=3 KnotsCount=2 Degree=2 IsPeriodic=0
    g130: BSplineCurve PolesCount=3 KnotsCount=2 Degree=2 IsPeriodic=0
    g131: BSplineCurve PolesCount=3 KnotsCount=2 Degree=2 IsPeriodic=0
    g132: BSplineCurve PolesCount=3 KnotsCount=2 Degree=2 IsPeriodic=0
    g133: BSplineCurve PolesCount=3 KnotsCount=2 Degree=2 IsPeriodic=0
    g134: BSplineCurve PolesCount=3 KnotsCount=2 Degree=2 IsPeriodic=0
    g135: BSplineCurve PolesCount=3 KnotsCount=2 Degree=2 IsPeriodic=0
    g136: BSplineCurve PolesCount=2 KnotsCount=2 Degree=1 IsPeriodic=0
    g137: BSplineCurve PolesCount=2 KnotsCount=2 Degree=1 IsPeriodic=0
    g138: BSplineCurve PolesCount=2 KnotsCount=2 Degree=1 IsPeriodic=0
    g139: BSplineCurve PolesCount=2 KnotsCount=2 Degree=1 IsPeriodic=0
    g140: BSplineCurve PolesCount=3 KnotsCount=2 Degree=2 IsPeriodic=0
    g141: BSplineCurve PolesCount=3 KnotsCount=2 Degree=2 IsPeriodic=0
    g142: BSplineCurve PolesCount=2 KnotsCount=2 Degree=1 IsPeriodic=0
    g143: BSplineCurve PolesCount=2 KnotsCount=2 Degree=1 IsPeriodic=0
    g144: BSplineCurve PolesCount=2 KnotsCount=2 Degree=1 IsPeriodic=0
    g145: BSplineCurve PolesCount=3 KnotsCount=2 Degree=2 IsPeriodic=0
    g146: BSplineCurve PolesCount=3 KnotsCount=2 Degree=2 IsPeriodic=0
    g147: BSplineCurve PolesCount=3 KnotsCount=2 Degree=2 IsPeriodic=0
    g148: BSplineCurve PolesCount=3 KnotsCount=2 Degree=2 IsPeriodic=0
    g149: BSplineCurve PolesCount=3 KnotsCount=2 Degree=2 IsPeriodic=0
    g150: BSplineCurve PolesCount=2 KnotsCount=2 Degree=1 IsPeriodic=0
    g151: BSplineCurve PolesCount=3 KnotsCount=2 Degree=2 IsPeriodic=0
    g152: BSplineCurve PolesCount=3 KnotsCount=2 Degree=2 IsPeriodic=0
    g153: BSplineCurve PolesCount=2 KnotsCount=2 Degree=1 IsPeriodic=0
    g154: BSplineCurve PolesCount=2 KnotsCount=2 Degree=1 IsPeriodic=0
    g155: BSplineCurve PolesCount=2 KnotsCount=2 Degree=1 IsPeriodic=0
    g156: BSplineCurve PolesCount=3 KnotsCount=2 Degree=2 IsPeriodic=0
    g157: BSplineCurve PolesCount=3 KnotsCount=2 Degree=2 IsPeriodic=0
    g158: BSplineCurve PolesCount=2 KnotsCount=2 Degree=1 IsPeriodic=0
    g159: BSplineCurve PolesCount=2 KnotsCount=2 Degree=1 IsPeriodic=0
    g160: BSplineCurve PolesCount=2 KnotsCount=2 Degree=1 IsPeriodic=0
    g161: BSplineCurve PolesCount=2 KnotsCount=2 Degree=1 IsPeriodic=0
    g162: BSplineCurve PolesCount=2 KnotsCount=2 Degree=1 IsPeriodic=0
    g163: BSplineCurve PolesCount=3 KnotsCount=2 Degree=2 IsPeriodic=0
    g164: BSplineCurve PolesCount=3 KnotsCount=2 Degree=2 IsPeriodic=0
    g165: BSplineCurve PolesCount=3 KnotsCount=2 Degree=2 IsPeriodic=0
    g166: BSplineCurve PolesCount=3 KnotsCount=2 Degree=2 IsPeriodic=0
    g167: BSplineCurve PolesCount=3 KnotsCount=2 Degree=2 IsPeriodic=0
    g168: BSplineCurve PolesCount=3 KnotsCount=2 Degree=2 IsPeriodic=0
    g169: BSplineCurve PolesCount=3 KnotsCount=2 Degree=2 IsPeriodic=0
    g170: BSplineCurve PolesCount=2 KnotsCount=2 Degree=1 IsPeriodic=0
    g171: BSplineCurve PolesCount=3 KnotsCount=2 Degree=2 IsPeriodic=0
    g172: BSplineCurve PolesCount=3 KnotsCount=2 Degree=2 IsPeriodic=0
    g173: BSplineCurve PolesCount=3 KnotsCount=2 Degree=2 IsPeriodic=0
    g174: BSplineCurve PolesCount=3 KnotsCount=2 Degree=2 IsPeriodic=0
    g175: BSplineCurve PolesCount=3 KnotsCount=2 Degree=2 IsPeriodic=0
    g176: BSplineCurve PolesCount=3 KnotsCount=2 Degree=2 IsPeriodic=0
    g177: BSplineCurve PolesCount=3 KnotsCount=2 Degree=2 IsPeriodic=0
    g178: BSplineCurve PolesCount=2 KnotsCount=2 Degree=1 IsPeriodic=0
    g179: BSplineCurve PolesCount=2 KnotsCount=2 Degree=1 IsPeriodic=0
    g180: BSplineCurve PolesCount=2 KnotsCount=2 Degree=1 IsPeriodic=0
    g181: BSplineCurve PolesCount=2 KnotsCount=2 Degree=1 IsPeriodic=0
    g182: BSplineCurve PolesCount=2 KnotsCount=2 Degree=1 IsPeriodic=0
    g183: BSplineCurve PolesCount=2 KnotsCount=2 Degree=1 IsPeriodic=0
  constraints (192):
    c: Coincident(g0,g1)
    c: Coincident(g1,g2)
    c: Coincident(g2,g3)
    c: Coincident(g3,g0)
    c: Horizontal(g0)
    c: Horizontal(g2)
    c: Vertical(g1)
    c: Vertical(g3)
    c: DistanceX(g2,g2) = 277
    c: DistanceY(g1,g1) = 20.5548
    c: DistanceX(g0,g-1) = 0
    c: DistanceY(g0,g-1) = 0
    c: Coincident(g4,g5)
    c: Coincident(g5,g6)
    c: Coincident(g6,g7)
    c: Coincident(g7,g8)
    c: Coincident(g8,g9)
    c: Coincident(g9,g10)
    c: Coincident(g10,g11)
    c: Coincident(g11,g4)
    c: Coincident(g12,g13)
    c: Coincident(g13,g14)
    c: Coincident(g14,g15)
    c: Coincident(g15,g16)
    c: Coincident(g16,g17)
    c: Coincident(g17,g18)
    c: Coincident(g18,g19)
    c: Coincident(g19,g12)
    c: Coincident(g20,g21)
    c: Coincident(g21,g22)
    c: Coincident(g22,g23)
    c: Coincident(g23,g24)
    c: Coincident(g24,g25)
    c: Coincident(g25,g26)
    c: Coincident(g26,g27)
    c: Coincident(g27,g28)
    c: Coincident(g28,g29)
    c: Coincident(g29,g30)
    c: Coincident(g30,g31)
    c: Coincident(g31,g32)
    c: Coincident(g32,g33)
    c: Coincident(g33,g34)
    c: Coincident(g34,g35)
    c: Coincident(g35,g36)
    c: Coincident(g36,g37)
    c: Coincident(g37,g38)
    c: Coincident(g38,g39)
    c: Coincident(g39,g40)
    c: Coincident(g40,g41)
    c: Coincident(g41,g42)
    c: Coincident(g42,g43)
    c: Coincident(g43,g44)
    c: Coincident(g44,g45)
    c: Coincident(g45,g46)
    c: Coincident(g46,g20)
    c: Coincident(g47,g48)
    c: Coincident(g48,g49)
    c: Coincident(g49,g50)
    c: Coincident(g50,g51)
    c: Coincident(g51,g52)
    c: Coincident(g52,g53)
    c: Coincident(g53,g54)
    c: Coincident(g54,g55)
    c: Coincident(g55,g56)
    c: Coincident(g56,g57)
    c: Coincident(g57,g58)
    c: Coincident(g58,g59)
    c: Coincident(g59,g47)
    c: Coincident(g60,g61)
    c: Coincident(g61,g62)
    c: Coincident(g62,g63)
    c: Coincident(g63,g64)
    c: Coincident(g64,g65)
    c: Coincident(g65,g66)
    c: Coincident(g66,g67)
    c: Coincident(g67,g68)
    c: Coincident(g68,g69)
    c: Coincident(g69,g70)
    c: Coincident(g70,g71)
    c: Coincident(g71,g60)
    c: Coincident(g72,g73)
    c: Coincident(g73,g74)
    c: Coincident(g74,g75)
    c: Coincident(g75,g76)
    c: Coincident(g76,g77)
    c: Coincident(g77,g78)
    c: Coincident(g78,g79)
    c: Coincident(g79,g80)
    c: Coincident(g80,g81)
    c: Coincident(g81,g82)
    c: Coincident(g82,g83)
    c: Coincident(g83,g84)
    c: Coincident(g84,g85)
    c: Coincident(g85,g86)
    c: Coincident(g86,g87)
    c: Coincident(g87,g88)
    c: Coincident(g88,g89)
    c: Coincident(g89,g72)
    c: Coincident(g90,g91)
    c: Coincident(g91,g92)
    c: Coincident(g92,g93)
    c: Coincident(g93,g90)
    c: Coincident(g94,g95)
    c: Coincident(g95,g96)
    c: Coincident(g96,g97)
    c: Coincident(g97,g98)
    c: Coincident(g98,g99)
    c: Coincident(g99,g100)
    c: Coincident(g100,g101)
    c: Coincident(g101,g94)
    c: Coincident(g102,g103)
    c: Coincident(g103,g104)
    c: Coincident(g104,g105)
    c: Coincident(g105,g106)
    c: Coincident(g106,g107)
    c: Coincident(g107,g108)
    c: Coincident(g108,g109)
    c: Coincident(g109,g102)
    c: Coincident(g110,g111)
    c: Coincident(g111,g112)
    c: Coincident(g112,g113)
    c: Coincident(g113,g114)
    c: Coincident(g114,g115)
    c: Coincident(g115,g116)
    c: Coincident(g116,g117)
    c: Coincident(g117,g118)
    c: Coincident(g118,g119)
    c: Coincident(g119,g120)
    c: Coincident(g120,g121)
    c: Coincident(g121,g122)
    c: Coincident(g122,g123)
    c: Coincident(g123,g124)
    c: Coincident(g124,g125)
    c: Coincident(g125,g126)
    c: Coincident(g126,g127)
    c: Coincident(g127,g128)
    c: Coincident(g128,g129)
    c: Coincident(g129,g130)
    c: Coincident(g130,g131)
    c: Coincident(g131,g132)
    c: Coincident(g132,g133)
    c: Coincident(g133,g134)
    c: Coincident(g134,g135)
    c: Coincident(g135,g136)
    c: Coincident(g136,g110)
    c: Coincident(g137,g138)
    c: Coincident(g138,g139)
    c: Coincident(g139,g140)
    c: Coincident(g140,g141)
    c: Coincident(g141,g142)
    c: Coincident(g142,g143)
    c: Coincident(g143,g144)
    c: Coincident(g144,g145)
    c: Coincident(g145,g146)
    c: Coincident(g146,g147)
    c: Coincident(g147,g148)
    c: Coincident(g148,g149)
    c: Coincident(g149,g137)
    c: Coincident(g150,g151)
    c: Coincident(g151,g152)
    c: Coincident(g152,g153)
    c: Coincident(g153,g154)
    c: Coincident(g154,g155)
    c: Coincident(g155,g156)
    c: Coincident(g156,g157)
    c: Coincident(g157,g158)
    c: Coincident(g158,g159)
    c: Coincident(g159,g160)
    c: Coincident(g160,g161)
    c: Coincident(g161,g150)
    c: Coincident(g162,g163)
    c: Coincident(g163,g164)
    c: Coincident(g164,g165)
    c: Coincident(g165,g166)
    c: Coincident(g166,g167)
    c: Coincident(g167,g168)
    c: Coincident(g168,g169)
    c: Coincident(g169,g170)
    c: Coincident(g170,g171)
    c: Coincident(g171,g172)
    c: Coincident(g172,g173)
    c: Coincident(g173,g174)
    c: Coincident(g174,g175)
    c: Coincident(g175,g176)
    c: Coincident(g176,g177)
    c: Coincident(g177,g178)
    c: Coincident(g178,g179)
    c: Coincident(g179,g162)
    c: Coincident(g180,g181)
    c: Coincident(g181,g182)
    c: Coincident(g182,g183)
    c: Coincident(g183,g180)
FEATURE [Part::FeaturePython] Sketch_On_Surface  # WARN: FeaturePython — macro-defined, semantics opaque (R4)
  ConstructionBounds = true
  FillExtrusion = true
  FillFaces = true
  ReverseU = false
  ReverseV = false
  Sketch = -> Mapped_Sketch
  SwapUV = false
  Thickness = -5
FEATURE [Part::Cut] Cut015019  label="cono_letras"
  Base = -> Cut015018
  Tool = -> Sketch_On_Surface
FEATURE [Part::Box] Box010  label="Cube010"
  AttacherType = Attacher::AttachEngine3D
  Height = 25.45
  Length = 25
  Placement = pos=(45,-0.5,-3.45) rot=(0,0,1;0rad)
  Width = 1
FEATURE [Part::MultiFuse] Fusion  label="cortador002"
  Shapes = -> [Box,Box002,Box010]
FEATURE [Part::Cut] Cut  label="cilindros"
  Base = -> Cylinder001
  Tool = -> Cylinder
FEATURE [Part::Cut] Cut015021  label="taza_cafe_interior_2"
  Base = -> Cut
  Tool = -> Fusion
FEATURE [App::DocumentObjectGroup] Group006  label="interior001"
  Group = -> [Cut015021]
FEATURE [Part::Cut] Cut015022  label="cilindros_para_cafe_exterior"
  Base = -> Cylinder003
  Tool = -> Cylinder002
FEATURE [Part::Box] Box011  label="Cube011"
  AttacherType = Attacher::AttachEngine3D
  Height = 25.45
  Length = 25
  Placement = pos=(40,-0.5,-6) rot=(0,0,1;0rad)
  Width = 1
FEATURE [Part::MultiFuse] Fusion004
  Shapes = -> [Box003,Box004,Box011]
FEATURE [Sketcher::SketchObject] Mapped_Sketch001
  FullyConstrained = false
  Support = -> [Cut015022]
  sketch-geometry (184):
    g0: LineSegment StartX=0 StartY=-16 StartZ=0 EndX=349.345 EndY=-16 EndZ=0
    g1: LineSegment StartX=349.345 StartY=-16 StartZ=0 EndX=349.345 EndY=0 EndZ=0
    g2: LineSegment StartX=349.345 StartY=0 StartZ=0 EndX=0 EndY=0 EndZ=0
    g3: LineSegment StartX=0 StartY=0 StartZ=0 EndX=0 EndY=-16 EndZ=0
    g4: BSplineCurve PolesCount=2 KnotsCount=2 Degree=1 IsPeriodic=0
    g5: BSplineCurve PolesCount=3 KnotsCount=2 Degree=2 IsPeriodic=0
    g6: BSplineCurve PolesCount=3 KnotsCount=2 Degree=2 IsPeriodic=0
    g7: BSplineCurve PolesCount=3 KnotsCount=2 Degree=2 IsPeriodic=0
    g8: BSplineCurve PolesCount=3 KnotsCount=2 Degree=2 IsPeriodic=0
    g9: BSplineCurve PolesCount=3 KnotsCount=2 Degree=2 IsPeriodic=0
    g10: BSplineCurve PolesCount=3 KnotsCount=2 Degree=2 IsPeriodic=0
    g11: BSplineCurve PolesCount=2 KnotsCount=2 Degree=1 IsPeriodic=0
    g12: BSplineCurve PolesCount=3 KnotsCount=2 Degree=2 IsPeriodic=0
    g13: BSplineCurve PolesCount=2 KnotsCount=2 Degree=1 IsPeriodic=0
    g14: BSplineCurve PolesCount=2 KnotsCount=2 Degree=1 IsPeriodic=0
    g15: BSplineCurve PolesCount=3 KnotsCount=2 Degree=2 IsPeriodic=0
    g16: BSplineCurve PolesCount=3 KnotsCount=2 Degree=2 IsPeriodic=0
    g17: BSplineCurve PolesCount=3 KnotsCount=2 Degree=2 IsPeriodic=0
    g18: BSplineCurve PolesCount=3 KnotsCount=2 Degree=2 IsPeriodic=0
    g19: BSplineCurve PolesCount=3 KnotsCount=2 Degree=2 IsPeriodic=0
    g20: BSplineCurve PolesCount=2 KnotsCount=2 Degree=1 IsPeriodic=0
    g21: BSplineCurve PolesCount=2 KnotsCount=2 Degree=1 IsPeriodic=0
    g22: BSplineCurve PolesCount=2 KnotsCount=2 Degree=1 IsPeriodic=0
    g23: BSplineCurve PolesCount=3 KnotsCount=2 Degree=2 IsPeriodic=0
    g24: BSplineCurve PolesCount=2 KnotsCount=2 Degree=1 IsPeriodic=0
    g25: BSplineCurve PolesCount=2 KnotsCount=2 Degree=1 IsPeriodic=0
    g26: BSplineCurve PolesCount=2 KnotsCount=2 Degree=1 IsPeriodic=0
    g27: BSplineCurve PolesCount=3 KnotsCount=2 Degree=2 IsPeriodic=0
    g28: BSplineCurve PolesCount=3 KnotsCount=2 Degree=2 IsPeriodic=0
    g29: BSplineCurve PolesCount=3 KnotsCount=2 Degree=2 IsPeriodic=0
    g30: BSplineCurve PolesCount=3 KnotsCount=2 Degree=2 IsPeriodic=0
    g31: BSplineCurve PolesCount=3 KnotsCount=2 Degree=2 IsPeriodic=0
    g32: BSplineCurve PolesCount=2 KnotsCount=2 Degree=1 IsPeriodic=0
    g33: BSplineCurve PolesCount=2 KnotsCount=2 Degree=1 IsPeriodic=0
    g34: BSplineCurve PolesCount=2 KnotsCount=2 Degree=1 IsPeriodic=0
    g35: BSplineCurve PolesCount=3 KnotsCount=2 Degree=2 IsPeriodic=0
    g36: BSplineCurve PolesCount=2 KnotsCount=2 Degree=1 IsPeriodic=0
    g37: BSplineCurve PolesCount=2 KnotsCount=2 Degree=1 IsPeriodic=0
    g38: BSplineCurve PolesCount=2 KnotsCount=2 Degree=1 IsPeriodic=0
    g39: BSplineCurve PolesCount=3 KnotsCount=2 Degree=2 IsPeriodic=0
    g40: BSplineCurve PolesCount=3 KnotsCount=2 Degree=2 IsPeriodic=0
    g41: BSplineCurve PolesCount=3 KnotsCount=2 Degree=2 IsPeriodic=0
    g42: BSplineCurve PolesCount=3 KnotsCount=2 Degree=2 IsPeriodic=0
    g43: BSplineCurve PolesCount=3 KnotsCount=2 Degree=2 IsPeriodic=0
    g44: BSplineCurve PolesCount=3 KnotsCount=2 Degree=2 IsPeriodic=0
    g45: BSplineCurve PolesCount=3 KnotsCount=2 Degree=2 IsPeriodic=0
    g46: BSplineCurve PolesCount=2 KnotsCount=2 Degree=1 IsPeriodic=0
    g47: BSplineCurve PolesCount=2 KnotsCount=2 Degree=1 IsPeriodic=0
    g48: BSplineCurve PolesCount=2 KnotsCount=2 Degree=1 IsPeriodic=0
    g49: BSplineCurve PolesCount=2 KnotsCount=2 Degree=1 IsPeriodic=0
    g50: BSplineCurve PolesCount=3 KnotsCount=2 Degree=2 IsPeriodic=0
    g51: BSplineCurve PolesCount=3 KnotsCount=2 Degree=2 IsPeriodic=0
    g52: BSplineCurve PolesCount=2 KnotsCount=2 Degree=1 IsPeriodic=0
    g53: BSplineCurve PolesCount=2 KnotsCount=2 Degree=1 IsPeriodic=0
    g54: BSplineCurve PolesCount=2 KnotsCount=2 Degree=1 IsPeriodic=0
    g55: BSplineCurve PolesCount=3 KnotsCount=2 Degree=2 IsPeriodic=0
    g56: BSplineCurve PolesCount=3 KnotsCount=2 Degree=2 IsPeriodic=0
    g57: BSplineCurve PolesCount=3 KnotsCount=2 Degree=2 IsPeriodic=0
    g58: BSplineCurve PolesCount=3 KnotsCount=2 Degree=2 IsPeriodic=0
    g59: BSplineCurve PolesCount=3 KnotsCount=2 Degree=2 IsPeriodic=0
    g60: BSplineCurve PolesCount=2 KnotsCount=2 Degree=1 IsPeriodic=0
    g61: BSplineCurve PolesCount=3 KnotsCount=2 Degree=2 IsPeriodic=0
    g62: BSplineCurve PolesCount=3 KnotsCount=2 Degree=2 IsPeriodic=0
    g63: BSplineCurve PolesCount=2 KnotsCount=2 Degree=1 IsPeriodic=0
    g64: BSplineCurve PolesCount=2 KnotsCount=2 Degree=1 IsPeriodic=0
    g65: BSplineCurve PolesCount=2 KnotsCount=2 Degree=1 IsPeriodic=0
    g66: BSplineCurve PolesCount=3 KnotsCount=2 Degree=2 IsPeriodic=0
    g67: BSplineCurve PolesCount=3 KnotsCount=2 Degree=2 IsPeriodic=0
    g68: BSplineCurve PolesCount=2 KnotsCount=2 Degree=1 IsPeriodic=0
    g69: BSplineCurve PolesCount=2 KnotsCount=2 Degree=1 IsPeriodic=0
    g70: BSplineCurve PolesCount=2 KnotsCount=2 Degree=1 IsPeriodic=0
    g71: BSplineCurve PolesCount=2 KnotsCount=2 Degree=1 IsPeriodic=0
    g72: BSplineCurve PolesCount=2 KnotsCount=2 Degree=1 IsPeriodic=0
    g73: BSplineCurve PolesCount=3 KnotsCount=2 Degree=2 IsPeriodic=0
    g74: BSplineCurve PolesCount=3 KnotsCount=2 Degree=2 IsPeriodic=0
    g75: BSplineCurve PolesCount=3 KnotsCount=2 Degree=2 IsPeriodic=0
    g76: BSplineCurve PolesCount=3 KnotsCount=2 Degree=2 IsPeriodic=0
    g77: BSplineCurve PolesCount=3 KnotsCount=2 Degree=2 IsPeriodic=0
    g78: BSplineCurve PolesCount=3 KnotsCount=2 Degree=2 IsPeriodic=0
    g79: BSplineCurve PolesCount=3 KnotsCount=2 Degree=2 IsPeriodic=0
    g80: BSplineCurve PolesCount=2 KnotsCount=2 Degree=1 IsPeriodic=0
    g81: BSplineCurve PolesCount=3 KnotsCount=2 Degree=2 IsPeriodic=0
    g82: BSplineCurve PolesCount=3 KnotsCount=2 Degree=2 IsPeriodic=0
    g83: BSplineCurve PolesCount=3 KnotsCount=2 Degree=2 IsPeriodic=0
    g84: BSplineCurve PolesCount=3 KnotsCount=2 Degree=2 IsPeriodic=0
    g85: BSplineCurve PolesCount=3 KnotsCount=2 Degree=2 IsPeriodic=0
    g86: BSplineCurve PolesCount=3 KnotsCount=2 Degree=2 IsPeriodic=0
    g87: BSplineCurve PolesCount=3 KnotsCount=2 Degree=2 IsPeriodic=0
    g88: BSplineCurve PolesCount=2 KnotsCount=2 Degree=1 IsPeriodic=0
    g89: BSplineCurve PolesCount=2 KnotsCount=2 Degree=1 IsPeriodic=0
    g90: BSplineCurve PolesCount=2 KnotsCount=2 Degree=1 IsPeriodic=0
    g91: BSplineCurve PolesCount=2 KnotsCount=2 Degree=1 IsPeriodic=0
    g92: BSplineCurve PolesCount=2 KnotsCount=2 Degree=1 IsPeriodic=0
    g93: BSplineCurve PolesCount=2 KnotsCount=2 Degree=1 IsPeriodic=0
    g94: BSplineCurve PolesCount=2 KnotsCount=2 Degree=1 IsPeriodic=0
    g95: BSplineCurve PolesCount=3 KnotsCount=2 Degree=2 IsPeriodic=0
    g96: BSplineCurve PolesCount=3 KnotsCount=2 Degree=2 IsPeriodic=0
    g97: BSplineCurve PolesCount=3 KnotsCount=2 Degree=2 IsPeriodic=0
    g98: BSplineCurve PolesCount=3 KnotsCount=2 Degree=2 IsPeriodic=0
    g99: BSplineCurve PolesCount=3 KnotsCount=2 Degree=2 IsPeriodic=0
    g100: BSplineCurve PolesCount=3 KnotsCount=2 Degree=2 IsPeriodic=0
    g101: BSplineCurve PolesCount=2 KnotsCount=2 Degree=1 IsPeriodic=0
    g102: BSplineCurve PolesCount=3 KnotsCount=2 Degree=2 IsPeriodic=0
    g103: BSplineCurve PolesCount=2 KnotsCount=2 Degree=1 IsPeriodic=0
    g104: BSplineCurve PolesCount=2 KnotsCount=2 Degree=1 IsPeriodic=0
    g105: BSplineCurve PolesCount=3 KnotsCount=2 Degree=2 IsPeriodic=0
    g106: BSplineCurve PolesCount=3 KnotsCount=2 Degree=2 IsPeriodic=0
    g107: BSplineCurve PolesCount=3 KnotsCount=2 Degree=2 IsPeriodic=0
    g108: BSplineCurve PolesCount=3 KnotsCount=2 Degree=2 IsPeriodic=0
    g109: BSplineCurve PolesCount=3 KnotsCount=2 Degree=2 IsPeriodic=0
    g110: BSplineCurve PolesCount=2 KnotsCount=2 Degree=1 IsPeriodic=0
    g111: BSplineCurve PolesCount=2 KnotsCount=2 Degree=1 IsPeriodic=0
    g112: BSplineCurve PolesCount=2 KnotsCount=2 Degree=1 IsPeriodic=0
    g113: BSplineCurve PolesCount=3 KnotsCount=2 Degree=2 IsPeriodic=0
    g114: BSplineCurve PolesCount=2 KnotsCount=2 Degree=1 IsPeriodic=0
    g115: BSplineCurve PolesCount=2 KnotsCount=2 Degree=1 IsPeriodic=0
    g116: BSplineCurve PolesCount=2 KnotsCount=2 Degree=1 IsPeriodic=0
    g117: BSplineCurve PolesCount=3 KnotsCount=2 Degree=2 IsPeriodic=0
    g118: BSplineCurve PolesCount=3 KnotsCount=2 Degree=2 IsPeriodic=0
    g119: BSplineCurve PolesCount=3 KnotsCount=2 Degree=2 IsPeriodic=0
    g120: BSplineCurve PolesCount=3 KnotsCount=2 Degree=2 IsPeriodic=0
    g121: BSplineCurve PolesCount=3 KnotsCount=2 Degree=2 IsPeriodic=0
    g122: BSplineCurve PolesCount=2 KnotsCount=2 Degree=1 IsPeriodic=0
    g123: BSplineCurve PolesCount=2 KnotsCount=2 Degree=1 IsPeriodic=0
    g124: BSplineCurve PolesCount=2 KnotsCount=2 Degree=1 IsPeriodic=0
    g125: BSplineCurve PolesCount=3 KnotsCount=2 Degree=2 IsPeriodic=0
    g126: BSplineCurve PolesCount=2 KnotsCount=2 Degree=1 IsPeriodic=0
    g127: BSplineCurve PolesCount=2 KnotsCount=2 Degree=1 IsPeriodic=0
    g128: BSplineCurve PolesCount=2 KnotsCount=2 Degree=1 IsPeriodic=0
    g129: BSplineCurve PolesCount=3 KnotsCount=2 Degree=2 IsPeriodic=0
    g130: BSplineCurve PolesCount=3 KnotsCount=2 Degree=2 IsPeriodic=0
    g131: BSplineCurve PolesCount=3 KnotsCount=2 Degree=2 IsPeriodic=0
    g132: BSplineCurve PolesCount=3 KnotsCount=2 Degree=2 IsPeriodic=0
    g133: BSplineCurve PolesCount=3 KnotsCount=2 Degree=2 IsPeriodic=0
    g134: BSplineCurve PolesCount=3 KnotsCount=2 Degree=2 IsPeriodic=0
    g135: BSplineCurve PolesCount=3 KnotsCount=2 Degree=2 IsPeriodic=0
    g136: BSplineCurve PolesCount=2 KnotsCount=2 Degree=1 IsPeriodic=0
    g137: BSplineCurve PolesCount=2 KnotsCount=2 Degree=1 IsPeriodic=0
    g138: BSplineCurve PolesCount=2 KnotsCount=2 Degree=1 IsPeriodic=0
    g139: BSplineCurve PolesCount=2 KnotsCount=2 Degree=1 IsPeriodic=0
    g140: BSplineCurve PolesCount=3 KnotsCount=2 Degree=2 IsPeriodic=0
    g141: BSplineCurve PolesCount=3 KnotsCount=2 Degree=2 IsPeriodic=0
    g142: BSplineCurve PolesCount=2 KnotsCount=2 Degree=1 IsPeriodic=0
    g143: BSplineCurve PolesCount=2 KnotsCount=2 Degree=1 IsPeriodic=0
    g144: BSplineCurve PolesCount=2 KnotsCount=2 Degree=1 IsPeriodic=0
    g145: BSplineCurve PolesCount=3 KnotsCount=2 Degree=2 IsPeriodic=0
    g146: BSplineCurve PolesCount=3 KnotsCount=2 Degree=2 IsPeriodic=0
    g147: BSplineCurve PolesCount=3 KnotsCount=2 Degree=2 IsPeriodic=0
    g148: BSplineCurve PolesCount=3 KnotsCount=2 Degree=2 IsPeriodic=0
    g149: BSplineCurve PolesCount=3 KnotsCount=2 Degree=2 IsPeriodic=0
    g150: BSplineCurve PolesCount=2 KnotsCount=2 Degree=1 IsPeriodic=0
    g151: BSplineCurve PolesCount=3 KnotsCount=2 Degree=2 IsPeriodic=0
    g152: BSplineCurve PolesCount=3 KnotsCount=2 Degree=2 IsPeriodic=0
    g153: BSplineCurve PolesCount=2 KnotsCount=2 Degree=1 IsPeriodic=0
    g154: BSplineCurve PolesCount=2 KnotsCount=2 Degree=1 IsPeriodic=0
    g155: BSplineCurve PolesCount=2 KnotsCount=2 Degree=1 IsPeriodic=0
    g156: BSplineCurve PolesCount=3 KnotsCount=2 Degree=2 IsPeriodic=0
    g157: BSplineCurve PolesCount=3 KnotsCount=2 Degree=2 IsPeriodic=0
    g158: BSplineCurve PolesCount=2 KnotsCount=2 Degree=1 IsPeriodic=0
    g159: BSplineCurve PolesCount=2 KnotsCount=2 Degree=1 IsPeriodic=0
    g160: BSplineCurve PolesCount=2 KnotsCount=2 Degree=1 IsPeriodic=0
    g161: BSplineCurve PolesCount=2 KnotsCount=2 Degree=1 IsPeriodic=0
    g162: BSplineCurve PolesCount=2 KnotsCount=2 Degree=1 IsPeriodic=0
    g163: BSplineCurve PolesCount=3 KnotsCount=2 Degree=2 IsPeriodic=0
    g164: BSplineCurve PolesCount=3 KnotsCount=2 Degree=2 IsPeriodic=0
    g165: BSplineCurve PolesCount=3 KnotsCount=2 Degree=2 IsPeriodic=0
    g166: BSplineCurve PolesCount=3 KnotsCount=2 Degree=2 IsPeriodic=0
    g167: BSplineCurve PolesCount=3 KnotsCount=2 Degree=2 IsPeriodic=0
    g168: BSplineCurve PolesCount=3 KnotsCount=2 Degree=2 IsPeriodic=0
    g169: BSplineCurve PolesCount=3 KnotsCount=2 Degree=2 IsPeriodic=0
    g170: BSplineCurve PolesCount=2 KnotsCount=2 Degree=1 IsPeriodic=0
    g171: BSplineCurve PolesCount=3 KnotsCount=2 Degree=2 IsPeriodic=0
    g172: BSplineCurve PolesCount=3 KnotsCount=2 Degree=2 IsPeriodic=0
    g173: BSplineCurve PolesCount=3 KnotsCount=2 Degree=2 IsPeriodic=0
    g174: BSplineCurve PolesCount=3 KnotsCount=2 Degree=2 IsPeriodic=0
    g175: BSplineCurve PolesCount=3 KnotsCount=2 Degree=2 IsPeriodic=0
    g176: BSplineCurve PolesCount=3 KnotsCount=2 Degree=2 IsPeriodic=0
    g177: BSplineCurve PolesCount=3 KnotsCount=2 Degree=2 IsPeriodic=0
    g178: BSplineCurve PolesCount=2 KnotsCount=2 Degree=1 IsPeriodic=0
    g179: BSplineCurve PolesCount=2 KnotsCount=2 Degree=1 IsPeriodic=0
    g180: BSplineCurve PolesCount=2 KnotsCount=2 Degree=1 IsPeriodic=0
    g181: BSplineCurve PolesCount=2 KnotsCount=2 Degree=1 IsPeriodic=0
    g182: BSplineCurve PolesCount=2 KnotsCount=2 Degree=1 IsPeriodic=0
    g183: BSplineCurve PolesCount=2 KnotsCount=2 Degree=1 IsPeriodic=0
  constraints (192):
    c: Coincident(g0,g1)
    c: Coincident(g1,g2)
    c: Coincident(g2,g3)
    c: Coincident(g3,g0)
    c: Horizontal(g0)
    c: Horizontal(g2)
    c: Vertical(g1)
    c: Vertical(g3)
    c: DistanceX(g2,g2) = 349.345
    c: DistanceY(g1,g1) = 16
    c: DistanceX(g0,g-1) = 0
    c: DistanceY(g0,g-1) = 16
    c: Coincident(g4,g5)
    c: Coincident(g5,g6)
    c: Coincident(g6,g7)
    c: Coincident(g7,g8)
    c: Coincident(g8,g9)
    c: Coincident(g9,g10)
    c: Coincident(g10,g11)
    c: Coincident(g11,g4)
    c: Coincident(g12,g13)
    c: Coincident(g13,g14)
    c: Coincident(g14,g15)
    c: Coincident(g15,g16)
    c: Coincident(g16,g17)
    c: Coincident(g17,g18)
    c: Coincident(g18,g19)
    c: Coincident(g19,g12)
    c: Coincident(g20,g21)
    c: Coincident(g21,g22)
    c: Coincident(g22,g23)
    c: Coincident(g23,g24)
    c: Coincident(g24,g25)
    c: Coincident(g25,g26)
    c: Coincident(g26,g27)
    c: Coincident(g27,g28)
    c: Coincident(g28,g29)
    c: Coincident(g29,g30)
    c: Coincident(g30,g31)
    c: Coincident(g31,g32)
    c: Coincident(g32,g33)
    c: Coincident(g33,g34)
    c: Coincident(g34,g35)
    c: Coincident(g35,g36)
    c: Coincident(g36,g37)
    c: Coincident(g37,g38)
    c: Coincident(g38,g39)
    c: Coincident(g39,g40)
    c: Coincident(g40,g41)
    c: Coincident(g41,g42)
    c: Coincident(g42,g43)
    c: Coincident(g43,g44)
    c: Coincident(g44,g45)
    c: Coincident(g45,g46)
    c: Coincident(g46,g20)
    c: Coincident(g47,g48)
    c: Coincident(g48,g49)
    c: Coincident(g49,g50)
    c: Coincident(g50,g51)
    c: Coincident(g51,g52)
    c: Coincident(g52,g53)
    c: Coincident(g53,g54)
    c: Coincident(g54,g55)
    c: Coincident(g55,g56)
    c: Coincident(g56,g57)
    c: Coincident(g57,g58)
    c: Coincident(g58,g59)
    c: Coincident(g59,g47)
    c: Coincident(g60,g61)
    c: Coincident(g61,g62)
    c: Coincident(g62,g63)
    c: Coincident(g63,g64)
    c: Coincident(g64,g65)
    c: Coincident(g65,g66)
    c: Coincident(g66,g67)
    c: Coincident(g67,g68)
    c: Coincident(g68,g69)
    c: Coincident(g69,g70)
    c: Coincident(g70,g71)
    c: Coincident(g71,g60)
    c: Coincident(g72,g73)
    c: Coincident(g73,g74)
    c: Coincident(g74,g75)
    c: Coincident(g75,g76)
    c: Coincident(g76,g77)
    c: Coincident(g77,g78)
    c: Coincident(g78,g79)
    c: Coincident(g79,g80)
    c: Coincident(g80,g81)
    c: Coincident(g81,g82)
    c: Coincident(g82,g83)
    c: Coincident(g83,g84)
    c: Coincident(g84,g85)
    c: Coincident(g85,g86)
    c: Coincident(g86,g87)
    c: Coincident(g87,g88)
    c: Coincident(g88,g89)
    c: Coincident(g89,g72)
    c: Coincident(g90,g91)
    c: Coincident(g91,g92)
    c: Coincident(g92,g93)
    c: Coincident(g93,g90)
    c: Coincident(g94,g95)
    c: Coincident(g95,g96)
    c: Coincident(g96,g97)
    c: Coincident(g97,g98)
    c: Coincident(g98,g99)
    c: Coincident(g99,g100)
    c: Coincident(g100,g101)
    c: Coincident(g101,g94)
    c: Coincident(g102,g103)
    c: Coincident(g103,g104)
    c: Coincident(g104,g105)
    c: Coincident(g105,g106)
    c: Coincident(g106,g107)
    c: Coincident(g107,g108)
    c: Coincident(g108,g109)
    c: Coincident(g109,g102)
    c: Coincident(g110,g111)
    c: Coincident(g111,g112)
    c: Coincident(g112,g113)
    c: Coincident(g113,g114)
    c: Coincident(g114,g115)
    c: Coincident(g115,g116)
    c: Coincident(g116,g117)
    c: Coincident(g117,g118)
    c: Coincident(g118,g119)
    c: Coincident(g119,g120)
    c: Coincident(g120,g121)
    c: Coincident(g121,g122)
    c: Coincident(g122,g123)
    c: Coincident(g123,g124)
    c: Coincident(g124,g125)
    c: Coincident(g125,g126)
    c: Coincident(g126,g127)
    c: Coincident(g127,g128)
    c: Coincident(g128,g129)
    c: Coincident(g129,g130)
    c: Coincident(g130,g131)
    c: Coincident(g131,g132)
    c: Coincident(g132,g133)
    c: Coincident(g133,g134)
    c: Coincident(g134,g135)
    c: Coincident(g135,g136)
    c: Coincident(g136,g110)
    c: Coincident(g137,g138)
    c: Coincident(g138,g139)
    c: Coincident(g139,g140)
    c: Coincident(g140,g141)
    c: Coincident(g141,g142)
    c: Coincident(g142,g143)
    c: Coincident(g143,g144)
    c: Coincident(g144,g145)
    c: Coincident(g145,g146)
    c: Coincident(g146,g147)
    c: Coincident(g147,g148)
    c: Coincident(g148,g149)
    c: Coincident(g149,g137)
    c: Coincident(g150,g151)
    c: Coincident(g151,g152)
    c: Coincident(g152,g153)
    c: Coincident(g153,g154)
    c: Coincident(g154,g155)
    c: Coincident(g155,g156)
    c: Coincident(g156,g157)
    c: Coincident(g157,g158)
    c: Coincident(g158,g159)
    c: Coincident(g159,g160)
    c: Coincident(g160,g161)
    c: Coincident(g161,g150)
    c: Coincident(g162,g163)
    c: Coincident(g163,g164)
    c: Coincident(g164,g165)
    c: Coincident(g165,g166)
    c: Coincident(g166,g167)
    c: Coincident(g167,g168)
    c: Coincident(g168,g169)
    c: Coincident(g169,g170)
    c: Coincident(g170,g171)
    c: Coincident(g171,g172)
    c: Coincident(g172,g173)
    c: Coincident(g173,g174)
    c: Coincident(g174,g175)
    c: Coincident(g175,g176)
    c: Coincident(g176,g177)
    c: Coincident(g177,g178)
    c: Coincident(g178,g179)
    c: Coincident(g179,g162)
    c: Coincident(g180,g181)
    c: Coincident(g181,g182)
    c: Coincident(g182,g183)
    c: Coincident(g183,g180)
FEATURE [Part::FeaturePython] Sketch_On_Surface001  # WARN: FeaturePython — macro-defined, semantics opaque (R4)
  ConstructionBounds = true
  FillExtrusion = true
  FillFaces = false
  ReverseU = false
  ReverseV = false
  Sketch = -> Mapped_Sketch001
  SwapUV = false
  Thickness = -6
FEATURE [Part::Feature] Compound005001  label="2_ernesto002"
  Placement = pos=(2.55,-16,0) rot=(1,0,0;3.14159rad)
  shape: bbox 229.5 x 10 x 2.467e-07 mm, 12 faces, 0 solids (baked)
FEATURE [Sketcher::SketchObject] Sketch001
  FullyConstrained = false
  sketch-geometry (180):
    g0: BSplineCurve PolesCount=2 KnotsCount=2 Degree=1 IsPeriodic=0
    g1: BSplineCurve PolesCount=3 KnotsCount=2 Degree=2 IsPeriodic=0
    g2: BSplineCurve PolesCount=3 KnotsCount=2 Degree=2 IsPeriodic=0
    g3: BSplineCurve PolesCount=3 KnotsCount=2 Degree=2 IsPeriodic=0
    g4: BSplineCurve PolesCount=3 KnotsCount=2 Degree=2 IsPeriodic=0
    g5: BSplineCurve PolesCount=3 KnotsCount=2 Degree=2 IsPeriodic=0
    g6: BSplineCurve PolesCount=3 KnotsCount=2 Degree=2 IsPeriodic=0
    g7: BSplineCurve PolesCount=2 KnotsCount=2 Degree=1 IsPeriodic=0
    g8: BSplineCurve PolesCount=3 KnotsCount=2 Degree=2 IsPeriodic=0
    g9: BSplineCurve PolesCount=2 KnotsCount=2 Degree=1 IsPeriodic=0
    g10: BSplineCurve PolesCount=2 KnotsCount=2 Degree=1 IsPeriodic=0
    g11: BSplineCurve PolesCount=3 KnotsCount=2 Degree=2 IsPeriodic=0
    g12: BSplineCurve PolesCount=3 KnotsCount=2 Degree=2 IsPeriodic=0
    g13: BSplineCurve PolesCount=3 KnotsCount=2 Degree=2 IsPeriodic=0
    g14: BSplineCurve PolesCount=3 KnotsCount=2 Degree=2 IsPeriodic=0
    g15: BSplineCurve PolesCount=3 KnotsCount=2 Degree=2 IsPeriodic=0
    g16: BSplineCurve PolesCount=2 KnotsCount=2 Degree=1 IsPeriodic=0
    g17: BSplineCurve PolesCount=2 KnotsCount=2 Degree=1 IsPeriodic=0
    g18: BSplineCurve PolesCount=2 KnotsCount=2 Degree=1 IsPeriodic=0
    g19: BSplineCurve PolesCount=3 KnotsCount=2 Degree=2 IsPeriodic=0
    g20: BSplineCurve PolesCount=2 KnotsCount=2 Degree=1 IsPeriodic=0
    g21: BSplineCurve PolesCount=2 KnotsCount=2 Degree=1 IsPeriodic=0
    g22: BSplineCurve PolesCount=2 KnotsCount=2 Degree=1 IsPeriodic=0
    g23: BSplineCurve PolesCount=3 KnotsCount=2 Degree=2 IsPeriodic=0
    g24: BSplineCurve PolesCount=3 KnotsCount=2 Degree=2 IsPeriodic=0
    g25: BSplineCurve PolesCount=3 KnotsCount=2 Degree=2 IsPeriodic=0
    g26: BSplineCurve PolesCount=3 KnotsCount=2 Degree=2 IsPeriodic=0
    g27: BSplineCurve PolesCount=3 KnotsCount=2 Degree=2 IsPeriodic=0
    g28: BSplineCurve PolesCount=2 KnotsCount=2 Degree=1 IsPeriodic=0
    g29: BSplineCurve PolesCount=2 KnotsCount=2 Degree=1 IsPeriodic=0
    g30: BSplineCurve PolesCount=2 KnotsCount=2 Degree=1 IsPeriodic=0
    g31: BSplineCurve PolesCount=3 KnotsCount=2 Degree=2 IsPeriodic=0
    g32: BSplineCurve PolesCount=2 KnotsCount=2 Degree=1 IsPeriodic=0
    g33: BSplineCurve PolesCount=2 KnotsCount=2 Degree=1 IsPeriodic=0
    g34: BSplineCurve PolesCount=2 KnotsCount=2 Degree=1 IsPeriodic=0
    g35: BSplineCurve PolesCount=3 KnotsCount=2 Degree=2 IsPeriodic=0
    g36: BSplineCurve PolesCount=3 KnotsCount=2 Degree=2 IsPeriodic=0
    g37: BSplineCurve PolesCount=3 KnotsCount=2 Degree=2 IsPeriodic=0
    g38: BSplineCurve PolesCount=3 KnotsCount=2 Degree=2 IsPeriodic=0
    g39: BSplineCurve PolesCount=3 KnotsCount=2 Degree=2 IsPeriodic=0
    g40: BSplineCurve PolesCount=3 KnotsCount=2 Degree=2 IsPeriodic=0
    g41: BSplineCurve PolesCount=3 KnotsCount=2 Degree=2 IsPeriodic=0
    g42: BSplineCurve PolesCount=2 KnotsCount=2 Degree=1 IsPeriodic=0
    g43: BSplineCurve PolesCount=2 KnotsCount=2 Degree=1 IsPeriodic=0
    g44: BSplineCurve PolesCount=2 KnotsCount=2 Degree=1 IsPeriodic=0
    g45: BSplineCurve PolesCount=2 KnotsCount=2 Degree=1 IsPeriodic=0
    g46: BSplineCurve PolesCount=3 KnotsCount=2 Degree=2 IsPeriodic=0
    g47: BSplineCurve PolesCount=3 KnotsCount=2 Degree=2 IsPeriodic=0
    g48: BSplineCurve PolesCount=2 KnotsCount=2 Degree=1 IsPeriodic=0
    g49: BSplineCurve PolesCount=2 KnotsCount=2 Degree=1 IsPeriodic=0
    g50: BSplineCurve PolesCount=2 KnotsCount=2 Degree=1 IsPeriodic=0
    g51: BSplineCurve PolesCount=3 KnotsCount=2 Degree=2 IsPeriodic=0
    g52: BSplineCurve PolesCount=3 KnotsCount=2 Degree=2 IsPeriodic=0
    g53: BSplineCurve PolesCount=3 KnotsCount=2 Degree=2 IsPeriodic=0
    g54: BSplineCurve PolesCount=3 KnotsCount=2 Degree=2 IsPeriodic=0
    g55: BSplineCurve PolesCount=3 KnotsCount=2 Degree=2 IsPeriodic=0
    g56: BSplineCurve PolesCount=2 KnotsCount=2 Degree=1 IsPeriodic=0
    g57: BSplineCurve PolesCount=3 KnotsCount=2 Degree=2 IsPeriodic=0
    g58: BSplineCurve PolesCount=3 KnotsCount=2 Degree=2 IsPeriodic=0
    g59: BSplineCurve PolesCount=2 KnotsCount=2 Degree=1 IsPeriodic=0
    g60: BSplineCurve PolesCount=2 KnotsCount=2 Degree=1 IsPeriodic=0
    g61: BSplineCurve PolesCount=2 KnotsCount=2 Degree=1 IsPeriodic=0
    g62: BSplineCurve PolesCount=3 KnotsCount=2 Degree=2 IsPeriodic=0
    g63: BSplineCurve PolesCount=3 KnotsCount=2 Degree=2 IsPeriodic=0
    g64: BSplineCurve PolesCount=2 KnotsCount=2 Degree=1 IsPeriodic=0
    g65: BSplineCurve PolesCount=2 KnotsCount=2 Degree=1 IsPeriodic=0
    g66: BSplineCurve PolesCount=2 KnotsCount=2 Degree=1 IsPeriodic=0
    g67: BSplineCurve PolesCount=2 KnotsCount=2 Degree=1 IsPeriodic=0
    g68: BSplineCurve PolesCount=2 KnotsCount=2 Degree=1 IsPeriodic=0
    g69: BSplineCurve PolesCount=3 KnotsCount=2 Degree=2 IsPeriodic=0
    g70: BSplineCurve PolesCount=3 KnotsCount=2 Degree=2 IsPeriodic=0
    g71: BSplineCurve PolesCount=3 KnotsCount=2 Degree=2 IsPeriodic=0
    g72: BSplineCurve PolesCount=3 KnotsCount=2 Degree=2 IsPeriodic=0
    g73: BSplineCurve PolesCount=3 KnotsCount=2 Degree=2 IsPeriodic=0
    g74: BSplineCurve PolesCount=3 KnotsCount=2 Degree=2 IsPeriodic=0
    g75: BSplineCurve PolesCount=3 KnotsCount=2 Degree=2 IsPeriodic=0
    g76: BSplineCurve PolesCount=2 KnotsCount=2 Degree=1 IsPeriodic=0
    g77: BSplineCurve PolesCount=3 KnotsCount=2 Degree=2 IsPeriodic=0
    g78: BSplineCurve PolesCount=3 KnotsCount=2 Degree=2 IsPeriodic=0
    g79: BSplineCurve PolesCount=3 KnotsCount=2 Degree=2 IsPeriodic=0
    g80: BSplineCurve PolesCount=3 KnotsCount=2 Degree=2 IsPeriodic=0
    g81: BSplineCurve PolesCount=3 KnotsCount=2 Degree=2 IsPeriodic=0
    g82: BSplineCurve PolesCount=3 KnotsCount=2 Degree=2 IsPeriodic=0
    g83: BSplineCurve PolesCount=3 KnotsCount=2 Degree=2 IsPeriodic=0
    g84: BSplineCurve PolesCount=2 KnotsCount=2 Degree=1 IsPeriodic=0
    g85: BSplineCurve PolesCount=2 KnotsCount=2 Degree=1 IsPeriodic=0
    g86: BSplineCurve PolesCount=2 KnotsCount=2 Degree=1 IsPeriodic=0
    g87: BSplineCurve PolesCount=2 KnotsCount=2 Degree=1 IsPeriodic=0
    g88: BSplineCurve PolesCount=2 KnotsCount=2 Degree=1 IsPeriodic=0
    g89: BSplineCurve PolesCount=2 KnotsCount=2 Degree=1 IsPeriodic=0
    g90: BSplineCurve PolesCount=2 KnotsCount=2 Degree=1 IsPeriodic=0
    g91: BSplineCurve PolesCount=3 KnotsCount=2 Degree=2 IsPeriodic=0
    g92: BSplineCurve PolesCount=3 KnotsCount=2 Degree=2 IsPeriodic=0
    g93: BSplineCurve PolesCount=3 KnotsCount=2 Degree=2 IsPeriodic=0
    g94: BSplineCurve PolesCount=3 KnotsCount=2 Degree=2 IsPeriodic=0
    g95: BSplineCurve PolesCount=3 KnotsCount=2 Degree=2 IsPeriodic=0
    g96: BSplineCurve PolesCount=3 KnotsCount=2 Degree=2 IsPeriodic=0
    g97: BSplineCurve PolesCount=2 KnotsCount=2 Degree=1 IsPeriodic=0
    g98: BSplineCurve PolesCount=3 KnotsCount=2 Degree=2 IsPeriodic=0
    g99: BSplineCurve PolesCount=2 KnotsCount=2 Degree=1 IsPeriodic=0
    g100: BSplineCurve PolesCount=2 KnotsCount=2 Degree=1 IsPeriodic=0
    g101: BSplineCurve PolesCount=3 KnotsCount=2 Degree=2 IsPeriodic=0
    g102: BSplineCurve PolesCount=3 KnotsCount=2 Degree=2 IsPeriodic=0
    g103: BSplineCurve PolesCount=3 KnotsCount=2 Degree=2 IsPeriodic=0
    g104: BSplineCurve PolesCount=3 KnotsCount=2 Degree=2 IsPeriodic=0
    g105: BSplineCurve PolesCount=3 KnotsCount=2 Degree=2 IsPeriodic=0
    g106: BSplineCurve PolesCount=2 KnotsCount=2 Degree=1 IsPeriodic=0
    g107: BSplineCurve PolesCount=2 KnotsCount=2 Degree=1 IsPeriodic=0
    g108: BSplineCurve PolesCount=2 KnotsCount=2 Degree=1 IsPeriodic=0
    g109: BSplineCurve PolesCount=3 KnotsCount=2 Degree=2 IsPeriodic=0
    g110: BSplineCurve PolesCount=2 KnotsCount=2 Degree=1 IsPeriodic=0
    g111: BSplineCurve PolesCount=2 KnotsCount=2 Degree=1 IsPeriodic=0
    g112: BSplineCurve PolesCount=2 KnotsCount=2 Degree=1 IsPeriodic=0
    g113: BSplineCurve PolesCount=3 KnotsCount=2 Degree=2 IsPeriodic=0
    g114: BSplineCurve PolesCount=3 KnotsCount=2 Degree=2 IsPeriodic=0
    g115: BSplineCurve PolesCount=3 KnotsCount=2 Degree=2 IsPeriodic=0
    g116: BSplineCurve PolesCount=3 KnotsCount=2 Degree=2 IsPeriodic=0
    g117: BSplineCurve PolesCount=3 KnotsCount=2 Degree=2 IsPeriodic=0
    g118: BSplineCurve PolesCount=2 KnotsCount=2 Degree=1 IsPeriodic=0
    g119: BSplineCurve PolesCount=2 KnotsCount=2 Degree=1 IsPeriodic=0
    g120: BSplineCurve PolesCount=2 KnotsCount=2 Degree=1 IsPeriodic=0
    g121: BSplineCurve PolesCount=3 KnotsCount=2 Degree=2 IsPeriodic=0
    g122: BSplineCurve PolesCount=2 KnotsCount=2 Degree=1 IsPeriodic=0
    g123: BSplineCurve PolesCount=2 KnotsCount=2 Degree=1 IsPeriodic=0
    g124: BSplineCurve PolesCount=2 KnotsCount=2 Degree=1 IsPeriodic=0
    g125: BSplineCurve PolesCount=3 KnotsCount=2 Degree=2 IsPeriodic=0
    g126: BSplineCurve PolesCount=3 KnotsCount=2 Degree=2 IsPeriodic=0
    g127: BSplineCurve PolesCount=3 KnotsCount=2 Degree=2 IsPeriodic=0
    g128: BSplineCurve PolesCount=3 KnotsCount=2 Degree=2 IsPeriodic=0
    g129: BSplineCurve PolesCount=3 KnotsCount=2 Degree=2 IsPeriodic=0
    g130: BSplineCurve PolesCount=3 KnotsCount=2 Degree=2 IsPeriodic=0
    g131: BSplineCurve PolesCount=3 KnotsCount=2 Degree=2 IsPeriodic=0
    g132: BSplineCurve PolesCount=2 KnotsCount=2 Degree=1 IsPeriodic=0
    g133: BSplineCurve PolesCount=2 KnotsCount=2 Degree=1 IsPeriodic=0
    g134: BSplineCurve PolesCount=2 KnotsCount=2 Degree=1 IsPeriodic=0
    g135: BSplineCurve PolesCount=2 KnotsCount=2 Degree=1 IsPeriodic=0
    g136: BSplineCurve PolesCount=3 KnotsCount=2 Degree=2 IsPeriodic=0
    g137: BSplineCurve PolesCount=3 KnotsCount=2 Degree=2 IsPeriodic=0
    g138: BSplineCurve PolesCount=2 KnotsCount=2 Degree=1 IsPeriodic=0
    g139: BSplineCurve PolesCount=2 KnotsCount=2 Degree=1 IsPeriodic=0
    g140: BSplineCurve PolesCount=2 KnotsCount=2 Degree=1 IsPeriodic=0
    g141: BSplineCurve PolesCount=3 KnotsCount=2 Degree=2 IsPeriodic=0
    g142: BSplineCurve PolesCount=3 KnotsCount=2 Degree=2 IsPeriodic=0
    g143: BSplineCurve PolesCount=3 KnotsCount=2 Degree=2 IsPeriodic=0
    g144: BSplineCurve PolesCount=3 KnotsCount=2 Degree=2 IsPeriodic=0
    g145: BSplineCurve PolesCount=3 KnotsCount=2 Degree=2 IsPeriodic=0
    g146: BSplineCurve PolesCount=2 KnotsCount=2 Degree=1 IsPeriodic=0
    g147: BSplineCurve PolesCount=3 KnotsCount=2 Degree=2 IsPeriodic=0
    g148: BSplineCurve PolesCount=3 KnotsCount=2 Degree=2 IsPeriodic=0
    g149: BSplineCurve PolesCount=2 KnotsCount=2 Degree=1 IsPeriodic=0
    g150: BSplineCurve PolesCount=2 KnotsCount=2 Degree=1 IsPeriodic=0
    g151: BSplineCurve PolesCount=2 KnotsCount=2 Degree=1 IsPeriodic=0
    g152: BSplineCurve PolesCount=3 KnotsCount=2 Degree=2 IsPeriodic=0
    g153: BSplineCurve PolesCount=3 KnotsCount=2 Degree=2 IsPeriodic=0
    g154: BSplineCurve PolesCount=2 KnotsCount=2 Degree=1 IsPeriodic=0
    g155: BSplineCurve PolesCount=2 KnotsCount=2 Degree=1 IsPeriodic=0
    g156: BSplineCurve PolesCount=2 KnotsCount=2 Degree=1 IsPeriodic=0
    g157: BSplineCurve PolesCount=2 KnotsCount=2 Degree=1 IsPeriodic=0
    g158: BSplineCurve PolesCount=2 KnotsCount=2 Degree=1 IsPeriodic=0
    g159: BSplineCurve PolesCount=3 KnotsCount=2 Degree=2 IsPeriodic=0
    g160: BSplineCurve PolesCount=3 KnotsCount=2 Degree=2 IsPeriodic=0
    g161: BSplineCurve PolesCount=3 KnotsCount=2 Degree=2 IsPeriodic=0
    g162: BSplineCurve PolesCount=3 KnotsCount=2 Degree=2 IsPeriodic=0
    g163: BSplineCurve PolesCount=3 KnotsCount=2 Degree=2 IsPeriodic=0
    g164: BSplineCurve PolesCount=3 KnotsCount=2 Degree=2 IsPeriodic=0
    g165: BSplineCurve PolesCount=3 KnotsCount=2 Degree=2 IsPeriodic=0
    g166: BSplineCurve PolesCount=2 KnotsCount=2 Degree=1 IsPeriodic=0
    g167: BSplineCurve PolesCount=3 KnotsCount=2 Degree=2 IsPeriodic=0
    g168: BSplineCurve PolesCount=3 KnotsCount=2 Degree=2 IsPeriodic=0
    g169: BSplineCurve PolesCount=3 KnotsCount=2 Degree=2 IsPeriodic=0
    g170: BSplineCurve PolesCount=3 KnotsCount=2 Degree=2 IsPeriodic=0
    g171: BSplineCurve PolesCount=3 KnotsCount=2 Degree=2 IsPeriodic=0
    g172: BSplineCurve PolesCount=3 KnotsCount=2 Degree=2 IsPeriodic=0
    g173: BSplineCurve PolesCount=3 KnotsCount=2 Degree=2 IsPeriodic=0
    g174: BSplineCurve PolesCount=2 KnotsCount=2 Degree=1 IsPeriodic=0
    g175: BSplineCurve PolesCount=2 KnotsCount=2 Degree=1 IsPeriodic=0
    g176: BSplineCurve PolesCount=2 KnotsCount=2 Degree=1 IsPeriodic=0
    g177: BSplineCurve PolesCount=2 KnotsCount=2 Degree=1 IsPeriodic=0
    g178: BSplineCurve PolesCount=2 KnotsCount=2 Degree=1 IsPeriodic=0
    g179: BSplineCurve PolesCount=2 KnotsCount=2 Degree=1 IsPeriodic=0
  constraints (180):
    c: Coincident(g0,g1)
    c: Coincident(g1,g2)
    c: Coincident(g2,g3)
    c: Coincident(g3,g4)
    c: Coincident(g4,g5)
    c: Coincident(g5,g6)
    c: Coincident(g6,g7)
    c: Coincident(g7,g0)
    c: Coincident(g8,g9)
    c: Coincident(g9,g10)
    c: Coincident(g10,g11)
    c: Coincident(g11,g12)
    c: Coincident(g12,g13)
    c: Coincident(g13,g14)
    c: Coincident(g14,g15)
    c: Coincident(g15,g8)
    c: Coincident(g16,g17)
    c: Coincident(g17,g18)
    c: Coincident(g18,g19)
    c: Coincident(g19,g20)
    c: Coincident(g20,g21)
    c: Coincident(g21,g22)
    c: Coincident(g22,g23)
    c: Coincident(g23,g24)
    c: Coincident(g24,g25)
    c: Coincident(g25,g26)
    c: Coincident(g26,g27)
    c: Coincident(g27,g28)
    c: Coincident(g28,g29)
    c: Coincident(g29,g30)
    c: Coincident(g30,g31)
    c: Coincident(g31,g32)
    c: Coincident(g32,g33)
    c: Coincident(g33,g34)
    c: Coincident(g34,g35)
    c: Coincident(g35,g36)
    c: Coincident(g36,g37)
    c: Coincident(g37,g38)
    c: Coincident(g38,g39)
    c: Coincident(g39,g40)
    c: Coincident(g40,g41)
    c: Coincident(g41,g42)
    c: Coincident(g42,g16)
    c: Coincident(g43,g44)
    c: Coincident(g44,g45)
    c: Coincident(g45,g46)
    c: Coincident(g46,g47)
    c: Coincident(g47,g48)
    c: Coincident(g48,g49)
    c: Coincident(g49,g50)
    c: Coincident(g50,g51)
    c: Coincident(g51,g52)
    c: Coincident(g52,g53)
    c: Coincident(g53,g54)
    c: Coincident(g54,g55)
    c: Coincident(g55,g43)
    c: Coincident(g56,g57)
    c: Coincident(g57,g58)
    c: Coincident(g58,g59)
    c: Coincident(g59,g60)
    c: Coincident(g60,g61)
    c: Coincident(g61,g62)
    c: Coincident(g62,g63)
    c: Coincident(g63,g64)
    c: Coincident(g64,g65)
    c: Coincident(g65,g66)
    c: Coincident(g66,g67)
    c: Coincident(g67,g56)
    c: Coincident(g68,g69)
    c: Coincident(g69,g70)
    c: Coincident(g70,g71)
    c: Coincident(g71,g72)
    c: Coincident(g72,g73)
    c: Coincident(g73,g74)
    c: Coincident(g74,g75)
    c: Coincident(g75,g76)
    c: Coincident(g76,g77)
    c: Coincident(g77,g78)
    c: Coincident(g78,g79)
    c: Coincident(g79,g80)
    c: Coincident(g80,g81)
    c: Coincident(g81,g82)
    c: Coincident(g82,g83)
    c: Coincident(g83,g84)
    c: Coincident(g84,g85)
    c: Coincident(g85,g68)
    c: Coincident(g86,g87)
    c: Coincident(g87,g88)
    c: Coincident(g88,g89)
    c: Coincident(g89,g86)
    c: Coincident(g90,g91)
    c: Coincident(g91,g92)
    c: Coincident(g92,g93)
    c: Coincident(g93,g94)
    c: Coincident(g94,g95)
    c: Coincident(g95,g96)
    c: Coincident(g96,g97)
    c: Coincident(g97,g90)
    c: Coincident(g98,g99)
    c: Coincident(g99,g100)
    c: Coincident(g100,g101)
    c: Coincident(g101,g102)
    c: Coincident(g102,g103)
    c: Coincident(g103,g104)
    c: Coincident(g104,g105)
    c: Coincident(g105,g98)
    c: Coincident(g106,g107)
    c: Coincident(g107,g108)
    c: Coincident(g108,g109)
    c: Coincident(g109,g110)
    c: Coincident(g110,g111)
    c: Coincident(g111,g112)
    c: Coincident(g112,g113)
    c: Coincident(g113,g114)
    c: Coincident(g114,g115)
    c: Coincident(g115,g116)
    c: Coincident(g116,g117)
    c: Coincident(g117,g118)
    c: Coincident(g118,g119)
    c: Coincident(g119,g120)
    c: Coincident(g120,g121)
    c: Coincident(g121,g122)
    c: Coincident(g122,g123)
    c: Coincident(g123,g124)
    c: Coincident(g124,g125)
    c: Coincident(g125,g126)
    c: Coincident(g126,g127)
    c: Coincident(g127,g128)
    c: Coincident(g128,g129)
    c: Coincident(g129,g130)
    c: Coincident(g130,g131)
    c: Coincident(g131,g132)
    c: Coincident(g132,g106)
    c: Coincident(g133,g134)
    c: Coincident(g134,g135)
    c: Coincident(g135,g136)
    c: Coincident(g136,g137)
    c: Coincident(g137,g138)
    c: Coincident(g138,g139)
    c: Coincident(g139,g140)
    c: Coincident(g140,g141)
    c: Coincident(g141,g142)
    c: Coincident(g142,g143)
    c: Coincident(g143,g144)
    c: Coincident(g144,g145)
    c: Coincident(g145,g133)
    c: Coincident(g146,g147)
    c: Coincident(g147,g148)
    c: Coincident(g148,g149)
    c: Coincident(g149,g150)
    c: Coincident(g150,g151)
    c: Coincident(g151,g152)
    c: Coincident(g152,g153)
    c: Coincident(g153,g154)
    c: Coincident(g154,g155)
    c: Coincident(g155,g156)
    c: Coincident(g156,g157)
    c: Coincident(g157,g146)
    c: Coincident(g158,g159)
    c: Coincident(g159,g160)
    c: Coincident(g160,g161)
    c: Coincident(g161,g162)
    c: Coincident(g162,g163)
    c: Coincident(g163,g164)
    c: Coincident(g164,g165)
    c: Coincident(g165,g166)
    c: Coincident(g166,g167)
    c: Coincident(g167,g168)
    c: Coincident(g168,g169)
    c: Coincident(g169,g170)
    c: Coincident(g170,g171)
    c: Coincident(g171,g172)
    c: Coincident(g172,g173)
    c: Coincident(g173,g174)
    c: Coincident(g174,g175)
    c: Coincident(g175,g158)
    c: Coincident(g176,g177)
    c: Coincident(g177,g178)
    c: Coincident(g178,g179)
    c: Coincident(g179,g176)
FEATURE [Part::Cone] Cone004  label="Cone_chico002"
  Angle = 360
  AttacherType = Attacher::AttachEngine3D
  Height = 20.5
  Radius1 = 43.6
  Radius2 = 42.1
FEATURE [Part::Cone] Cone005  label="Cone001_grande002"
  Angle = 360
  AttacherType = Attacher::AttachEngine3D
  Height = 20.5
  Radius1 = 45.6
  Radius2 = 44.1
FEATURE [Part::Cut] Cut015023  label="cono001"
  Base = -> Cone005
  Tool = -> Cone004
FEATURE [App::DocumentObjectGroup] Group002  label="otros"
  Group = -> [Compound001,Compound,Face004,Face003,Cut015023]
FEATURE [Sketcher::SketchObject] Mapped_Sketch002
  FullyConstrained = false
  Support = -> [Cut015023]
  sketch-geometry (184):
    g0: LineSegment StartX=0 StartY=0 StartZ=0 EndX=277 EndY=0 EndZ=0
    g1: LineSegment StartX=277 StartY=0 StartZ=0 EndX=277 EndY=20.5548 EndZ=0
    g2: LineSegment StartX=277 StartY=20.5548 StartZ=0 EndX=0 EndY=20.5548 EndZ=0
    g3: LineSegment StartX=0 StartY=20.5548 StartZ=0 EndX=0 EndY=0 EndZ=0
    g4: BSplineCurve PolesCount=2 KnotsCount=2 Degree=1 IsPeriodic=0
    g5: BSplineCurve PolesCount=3 KnotsCount=2 Degree=2 IsPeriodic=0
    g6: BSplineCurve PolesCount=3 KnotsCount=2 Degree=2 IsPeriodic=0
    g7: BSplineCurve PolesCount=3 KnotsCount=2 Degree=2 IsPeriodic=0
    g8: BSplineCurve PolesCount=3 KnotsCount=2 Degree=2 IsPeriodic=0
    g9: BSplineCurve PolesCount=3 KnotsCount=2 Degree=2 IsPeriodic=0
    g10: BSplineCurve PolesCount=3 KnotsCount=2 Degree=2 IsPeriodic=0
    g11: BSplineCurve PolesCount=2 KnotsCount=2 Degree=1 IsPeriodic=0
    g12: BSplineCurve PolesCount=3 KnotsCount=2 Degree=2 IsPeriodic=0
    g13: BSplineCurve PolesCount=2 KnotsCount=2 Degree=1 IsPeriodic=0
    g14: BSplineCurve PolesCount=2 KnotsCount=2 Degree=1 IsPeriodic=0
    g15: BSplineCurve PolesCount=3 KnotsCount=2 Degree=2 IsPeriodic=0
    g16: BSplineCurve PolesCount=3 KnotsCount=2 Degree=2 IsPeriodic=0
    g17: BSplineCurve PolesCount=3 KnotsCount=2 Degree=2 IsPeriodic=0
    g18: BSplineCurve PolesCount=3 KnotsCount=2 Degree=2 IsPeriodic=0
    g19: BSplineCurve PolesCount=3 KnotsCount=2 Degree=2 IsPeriodic=0
    g20: BSplineCurve PolesCount=2 KnotsCount=2 Degree=1 IsPeriodic=0
    g21: BSplineCurve PolesCount=2 KnotsCount=2 Degree=1 IsPeriodic=0
    g22: BSplineCurve PolesCount=2 KnotsCount=2 Degree=1 IsPeriodic=0
    g23: BSplineCurve PolesCount=3 KnotsCount=2 Degree=2 IsPeriodic=0
    g24: BSplineCurve PolesCount=2 KnotsCount=2 Degree=1 IsPeriodic=0
    g25: BSplineCurve PolesCount=2 KnotsCount=2 Degree=1 IsPeriodic=0
    g26: BSplineCurve PolesCount=2 KnotsCount=2 Degree=1 IsPeriodic=0
    g27: BSplineCurve PolesCount=3 KnotsCount=2 Degree=2 IsPeriodic=0
    g28: BSplineCurve PolesCount=3 KnotsCount=2 Degree=2 IsPeriodic=0
    g29: BSplineCurve PolesCount=3 KnotsCount=2 Degree=2 IsPeriodic=0
    g30: BSplineCurve PolesCount=3 KnotsCount=2 Degree=2 IsPeriodic=0
    g31: BSplineCurve PolesCount=3 KnotsCount=2 Degree=2 IsPeriodic=0
    g32: BSplineCurve PolesCount=2 KnotsCount=2 Degree=1 IsPeriodic=0
    g33: BSplineCurve PolesCount=2 KnotsCount=2 Degree=1 IsPeriodic=0
    g34: BSplineCurve PolesCount=2 KnotsCount=2 Degree=1 IsPeriodic=0
    g35: BSplineCurve PolesCount=3 KnotsCount=2 Degree=2 IsPeriodic=0
    g36: BSplineCurve PolesCount=2 KnotsCount=2 Degree=1 IsPeriodic=0
    g37: BSplineCurve PolesCount=2 KnotsCount=2 Degree=1 IsPeriodic=0
    g38: BSplineCurve PolesCount=2 KnotsCount=2 Degree=1 IsPeriodic=0
    g39: BSplineCurve PolesCount=3 KnotsCount=2 Degree=2 IsPeriodic=0
    g40: BSplineCurve PolesCount=3 KnotsCount=2 Degree=2 IsPeriodic=0
    g41: BSplineCurve PolesCount=3 KnotsCount=2 Degree=2 IsPeriodic=0
    g42: BSplineCurve PolesCount=3 KnotsCount=2 Degree=2 IsPeriodic=0
    g43: BSplineCurve PolesCount=3 KnotsCount=2 Degree=2 IsPeriodic=0
    g44: BSplineCurve PolesCount=3 KnotsCount=2 Degree=2 IsPeriodic=0
    g45: BSplineCurve PolesCount=3 KnotsCount=2 Degree=2 IsPeriodic=0
    g46: BSplineCurve PolesCount=2 KnotsCount=2 Degree=1 IsPeriodic=0
    g47: BSplineCurve PolesCount=2 KnotsCount=2 Degree=1 IsPeriodic=0
    g48: BSplineCurve PolesCount=2 KnotsCount=2 Degree=1 IsPeriodic=0
    g49: BSplineCurve PolesCount=2 KnotsCount=2 Degree=1 IsPeriodic=0
    g50: BSplineCurve PolesCount=3 KnotsCount=2 Degree=2 IsPeriodic=0
    g51: BSplineCurve PolesCount=3 KnotsCount=2 Degree=2 IsPeriodic=0
    g52: BSplineCurve PolesCount=2 KnotsCount=2 Degree=1 IsPeriodic=0
    g53: BSplineCurve PolesCount=2 KnotsCount=2 Degree=1 IsPeriodic=0
    g54: BSplineCurve PolesCount=2 KnotsCount=2 Degree=1 IsPeriodic=0
    g55: BSplineCurve PolesCount=3 KnotsCount=2 Degree=2 IsPeriodic=0
    g56: BSplineCurve PolesCount=3 KnotsCount=2 Degree=2 IsPeriodic=0
    g57: BSplineCurve PolesCount=3 KnotsCount=2 Degree=2 IsPeriodic=0
    g58: BSplineCurve PolesCount=3 KnotsCount=2 Degree=2 IsPeriodic=0
    g59: BSplineCurve PolesCount=3 KnotsCount=2 Degree=2 IsPeriodic=0
    g60: BSplineCurve PolesCount=2 KnotsCount=2 Degree=1 IsPeriodic=0
    g61: BSplineCurve PolesCount=3 KnotsCount=2 Degree=2 IsPeriodic=0
    g62: BSplineCurve PolesCount=3 KnotsCount=2 Degree=2 IsPeriodic=0
    g63: BSplineCurve PolesCount=2 KnotsCount=2 Degree=1 IsPeriodic=0
    g64: BSplineCurve PolesCount=2 KnotsCount=2 Degree=1 IsPeriodic=0
    g65: BSplineCurve PolesCount=2 KnotsCount=2 Degree=1 IsPeriodic=0
    g66: BSplineCurve PolesCount=3 KnotsCount=2 Degree=2 IsPeriodic=0
    g67: BSplineCurve PolesCount=3 KnotsCount=2 Degree=2 IsPeriodic=0
    g68: BSplineCurve PolesCount=2 KnotsCount=2 Degree=1 IsPeriodic=0
    g69: BSplineCurve PolesCount=2 KnotsCount=2 Degree=1 IsPeriodic=0
    g70: BSplineCurve PolesCount=2 KnotsCount=2 Degree=1 IsPeriodic=0
    g71: BSplineCurve PolesCount=2 KnotsCount=2 Degree=1 IsPeriodic=0
    g72: BSplineCurve PolesCount=2 KnotsCount=2 Degree=1 IsPeriodic=0
    g73: BSplineCurve PolesCount=3 KnotsCount=2 Degree=2 IsPeriodic=0
    g74: BSplineCurve PolesCount=3 KnotsCount=2 Degree=2 IsPeriodic=0
    g75: BSplineCurve PolesCount=3 KnotsCount=2 Degree=2 IsPeriodic=0
    g76: BSplineCurve PolesCount=3 KnotsCount=2 Degree=2 IsPeriodic=0
    g77: BSplineCurve PolesCount=3 KnotsCount=2 Degree=2 IsPeriodic=0
    g78: BSplineCurve PolesCount=3 KnotsCount=2 Degree=2 IsPeriodic=0
    g79: BSplineCurve PolesCount=3 KnotsCount=2 Degree=2 IsPeriodic=0
    g80: BSplineCurve PolesCount=2 KnotsCount=2 Degree=1 IsPeriodic=0
    g81: BSplineCurve PolesCount=3 KnotsCount=2 Degree=2 IsPeriodic=0
    g82: BSplineCurve PolesCount=3 KnotsCount=2 Degree=2 IsPeriodic=0
    g83: BSplineCurve PolesCount=3 KnotsCount=2 Degree=2 IsPeriodic=0
    g84: BSplineCurve PolesCount=3 KnotsCount=2 Degree=2 IsPeriodic=0
    g85: BSplineCurve PolesCount=3 KnotsCount=2 Degree=2 IsPeriodic=0
    g86: BSplineCurve PolesCount=3 KnotsCount=2 Degree=2 IsPeriodic=0
    g87: BSplineCurve PolesCount=3 KnotsCount=2 Degree=2 IsPeriodic=0
    g88: BSplineCurve PolesCount=2 KnotsCount=2 Degree=1 IsPeriodic=0
    g89: BSplineCurve PolesCount=2 KnotsCount=2 Degree=1 IsPeriodic=0
    g90: BSplineCurve PolesCount=2 KnotsCount=2 Degree=1 IsPeriodic=0
    g91: BSplineCurve PolesCount=2 KnotsCount=2 Degree=1 IsPeriodic=0
    g92: BSplineCurve PolesCount=2 KnotsCount=2 Degree=1 IsPeriodic=0
    g93: BSplineCurve PolesCount=2 KnotsCount=2 Degree=1 IsPeriodic=0
    g94: BSplineCurve PolesCount=2 KnotsCount=2 Degree=1 IsPeriodic=0
    g95: BSplineCurve PolesCount=3 KnotsCount=2 Degree=2 IsPeriodic=0
    g96: BSplineCurve PolesCount=3 KnotsCount=2 Degree=2 IsPeriodic=0
    g97: BSplineCurve PolesCount=3 KnotsCount=2 Degree=2 IsPeriodic=0
    g98: BSplineCurve PolesCount=3 KnotsCount=2 Degree=2 IsPeriodic=0
    g99: BSplineCurve PolesCount=3 KnotsCount=2 Degree=2 IsPeriodic=0
    g100: BSplineCurve PolesCount=3 KnotsCount=2 Degree=2 IsPeriodic=0
    g101: BSplineCurve PolesCount=2 KnotsCount=2 Degree=1 IsPeriodic=0
    g102: BSplineCurve PolesCount=3 KnotsCount=2 Degree=2 IsPeriodic=0
    g103: BSplineCurve PolesCount=2 KnotsCount=2 Degree=1 IsPeriodic=0
    g104: BSplineCurve PolesCount=2 KnotsCount=2 Degree=1 IsPeriodic=0
    g105: BSplineCurve PolesCount=3 KnotsCount=2 Degree=2 IsPeriodic=0
    g106: BSplineCurve PolesCount=3 KnotsCount=2 Degree=2 IsPeriodic=0
    g107: BSplineCurve PolesCount=3 KnotsCount=2 Degree=2 IsPeriodic=0
    g108: BSplineCurve PolesCount=3 KnotsCount=2 Degree=2 IsPeriodic=0
    g109: BSplineCurve PolesCount=3 KnotsCount=2 Degree=2 IsPeriodic=0
    g110: BSplineCurve PolesCount=2 KnotsCount=2 Degree=1 IsPeriodic=0
    g111: BSplineCurve PolesCount=2 KnotsCount=2 Degree=1 IsPeriodic=0
    g112: BSplineCurve PolesCount=2 KnotsCount=2 Degree=1 IsPeriodic=0
    g113: BSplineCurve PolesCount=3 KnotsCount=2 Degree=2 IsPeriodic=0
    g114: BSplineCurve PolesCount=2 KnotsCount=2 Degree=1 IsPeriodic=0
    g115: BSplineCurve PolesCount=2 KnotsCount=2 Degree=1 IsPeriodic=0
    g116: BSplineCurve PolesCount=2 KnotsCount=2 Degree=1 IsPeriodic=0
    g117: BSplineCurve PolesCount=3 KnotsCount=2 Degree=2 IsPeriodic=0
    g118: BSplineCurve PolesCount=3 KnotsCount=2 Degree=2 IsPeriodic=0
    g119: BSplineCurve PolesCount=3 KnotsCount=2 Degree=2 IsPeriodic=0
    g120: BSplineCurve PolesCount=3 KnotsCount=2 Degree=2 IsPeriodic=0
    g121: BSplineCurve PolesCount=3 KnotsCount=2 Degree=2 IsPeriodic=0
    g122: BSplineCurve PolesCount=2 KnotsCount=2 Degree=1 IsPeriodic=0
    g123: BSplineCurve PolesCount=2 KnotsCount=2 Degree=1 IsPeriodic=0
    g124: BSplineCurve PolesCount=2 KnotsCount=2 Degree=1 IsPeriodic=0
    g125: BSplineCurve PolesCount=3 KnotsCount=2 Degree=2 IsPeriodic=0
    g126: BSplineCurve PolesCount=2 KnotsCount=2 Degree=1 IsPeriodic=0
    g127: BSplineCurve PolesCount=2 KnotsCount=2 Degree=1 IsPeriodic=0
    g128: BSplineCurve PolesCount=2 KnotsCount=2 Degree=1 IsPeriodic=0
    g129: BSplineCurve PolesCount=3 KnotsCount=2 Degree=2 IsPeriodic=0
    g130: BSplineCurve PolesCount=3 KnotsCount=2 Degree=2 IsPeriodic=0
    g131: BSplineCurve PolesCount=3 KnotsCount=2 Degree=2 IsPeriodic=0
    g132: BSplineCurve PolesCount=3 KnotsCount=2 Degree=2 IsPeriodic=0
    g133: BSplineCurve PolesCount=3 KnotsCount=2 Degree=2 IsPeriodic=0
    g134: BSplineCurve PolesCount=3 KnotsCount=2 Degree=2 IsPeriodic=0
    g135: BSplineCurve PolesCount=3 KnotsCount=2 Degree=2 IsPeriodic=0
    g136: BSplineCurve PolesCount=2 KnotsCount=2 Degree=1 IsPeriodic=0
    g137: BSplineCurve PolesCount=2 KnotsCount=2 Degree=1 IsPeriodic=0
    g138: BSplineCurve PolesCount=2 KnotsCount=2 Degree=1 IsPeriodic=0
    g139: BSplineCurve PolesCount=2 KnotsCount=2 Degree=1 IsPeriodic=0
    g140: BSplineCurve PolesCount=3 KnotsCount=2 Degree=2 IsPeriodic=0
    g141: BSplineCurve PolesCount=3 KnotsCount=2 Degree=2 IsPeriodic=0
    g142: BSplineCurve PolesCount=2 KnotsCount=2 Degree=1 IsPeriodic=0
    g143: BSplineCurve PolesCount=2 KnotsCount=2 Degree=1 IsPeriodic=0
    g144: BSplineCurve PolesCount=2 KnotsCount=2 Degree=1 IsPeriodic=0
    g145: BSplineCurve PolesCount=3 KnotsCount=2 Degree=2 IsPeriodic=0
    g146: BSplineCurve PolesCount=3 KnotsCount=2 Degree=2 IsPeriodic=0
    g147: BSplineCurve PolesCount=3 KnotsCount=2 Degree=2 IsPeriodic=0
    g148: BSplineCurve PolesCount=3 KnotsCount=2 Degree=2 IsPeriodic=0
    g149: BSplineCurve PolesCount=3 KnotsCount=2 Degree=2 IsPeriodic=0
    g150: BSplineCurve PolesCount=2 KnotsCount=2 Degree=1 IsPeriodic=0
    g151: BSplineCurve PolesCount=3 KnotsCount=2 Degree=2 IsPeriodic=0
    g152: BSplineCurve PolesCount=3 KnotsCount=2 Degree=2 IsPeriodic=0
    g153: BSplineCurve PolesCount=2 KnotsCount=2 Degree=1 IsPeriodic=0
    g154: BSplineCurve PolesCount=2 KnotsCount=2 Degree=1 IsPeriodic=0
    g155: BSplineCurve PolesCount=2 KnotsCount=2 Degree=1 IsPeriodic=0
    g156: BSplineCurve PolesCount=3 KnotsCount=2 Degree=2 IsPeriodic=0
    g157: BSplineCurve PolesCount=3 KnotsCount=2 Degree=2 IsPeriodic=0
    g158: BSplineCurve PolesCount=2 KnotsCount=2 Degree=1 IsPeriodic=0
    g159: BSplineCurve PolesCount=2 KnotsCount=2 Degree=1 IsPeriodic=0
    g160: BSplineCurve PolesCount=2 KnotsCount=2 Degree=1 IsPeriodic=0
    g161: BSplineCurve PolesCount=2 KnotsCount=2 Degree=1 IsPeriodic=0
    g162: BSplineCurve PolesCount=2 KnotsCount=2 Degree=1 IsPeriodic=0
    g163: BSplineCurve PolesCount=3 KnotsCount=2 Degree=2 IsPeriodic=0
    g164: BSplineCurve PolesCount=3 KnotsCount=2 Degree=2 IsPeriodic=0
    g165: BSplineCurve PolesCount=3 KnotsCount=2 Degree=2 IsPeriodic=0
    g166: BSplineCurve PolesCount=3 KnotsCount=2 Degree=2 IsPeriodic=0
    g167: BSplineCurve PolesCount=3 KnotsCount=2 Degree=2 IsPeriodic=0
    g168: BSplineCurve PolesCount=3 KnotsCount=2 Degree=2 IsPeriodic=0
    g169: BSplineCurve PolesCount=3 KnotsCount=2 Degree=2 IsPeriodic=0
    g170: BSplineCurve PolesCount=2 KnotsCount=2 Degree=1 IsPeriodic=0
    g171: BSplineCurve PolesCount=3 KnotsCount=2 Degree=2 IsPeriodic=0
    g172: BSplineCurve PolesCount=3 KnotsCount=2 Degree=2 IsPeriodic=0
    g173: BSplineCurve PolesCount=3 KnotsCount=2 Degree=2 IsPeriodic=0
    g174: BSplineCurve PolesCount=3 KnotsCount=2 Degree=2 IsPeriodic=0
    g175: BSplineCurve PolesCount=3 KnotsCount=2 Degree=2 IsPeriodic=0
    g176: BSplineCurve PolesCount=3 KnotsCount=2 Degree=2 IsPeriodic=0
    g177: BSplineCurve PolesCount=3 KnotsCount=2 Degree=2 IsPeriodic=0
    g178: BSplineCurve PolesCount=2 KnotsCount=2 Degree=1 IsPeriodic=0
    g179: BSplineCurve PolesCount=2 KnotsCount=2 Degree=1 IsPeriodic=0
    g180: BSplineCurve PolesCount=2 KnotsCount=2 Degree=1 IsPeriodic=0
    g181: BSplineCurve PolesCount=2 KnotsCount=2 Degree=1 IsPeriodic=0
    g182: BSplineCurve PolesCount=2 KnotsCount=2 Degree=1 IsPeriodic=0
    g183: BSplineCurve PolesCount=2 KnotsCount=2 Degree=1 IsPeriodic=0
  constraints (192):
    c: Coincident(g0,g1)
    c: Coincident(g1,g2)
    c: Coincident(g2,g3)
    c: Coincident(g3,g0)
    c: Horizontal(g0)
    c: Horizontal(g2)
    c: Vertical(g1)
    c: Vertical(g3)
    c: DistanceX(g2,g2) = 277
    c: DistanceY(g1,g1) = 20.5548
    c: DistanceX(g0,g-1) = 0
    c: DistanceY(g0,g-1) = 0
    c: Coincident(g4,g5)
    c: Coincident(g5,g6)
    c: Coincident(g6,g7)
    c: Coincident(g7,g8)
    c: Coincident(g8,g9)
    c: Coincident(g9,g10)
    c: Coincident(g10,g11)
    c: Coincident(g11,g4)
    c: Coincident(g12,g13)
    c: Coincident(g13,g14)
    c: Coincident(g14,g15)
    c: Coincident(g15,g16)
    c: Coincident(g16,g17)
    c: Coincident(g17,g18)
    c: Coincident(g18,g19)
    c: Coincident(g19,g12)
    c: Coincident(g20,g21)
    c: Coincident(g21,g22)
    c: Coincident(g22,g23)
    c: Coincident(g23,g24)
    c: Coincident(g24,g25)
    c: Coincident(g25,g26)
    c: Coincident(g26,g27)
    c: Coincident(g27,g28)
    c: Coincident(g28,g29)
    c: Coincident(g29,g30)
    c: Coincident(g30,g31)
    c: Coincident(g31,g32)
    c: Coincident(g32,g33)
    c: Coincident(g33,g34)
    c: Coincident(g34,g35)
    c: Coincident(g35,g36)
    c: Coincident(g36,g37)
    c: Coincident(g37,g38)
    c: Coincident(g38,g39)
    c: Coincident(g39,g40)
    c: Coincident(g40,g41)
    c: Coincident(g41,g42)
    c: Coincident(g42,g43)
    c: Coincident(g43,g44)
    c: Coincident(g44,g45)
    c: Coincident(g45,g46)
    c: Coincident(g46,g20)
    c: Coincident(g47,g48)
    c: Coincident(g48,g49)
    c: Coincident(g49,g50)
    c: Coincident(g50,g51)
    c: Coincident(g51,g52)
    c: Coincident(g52,g53)
    c: Coincident(g53,g54)
    c: Coincident(g54,g55)
    c: Coincident(g55,g56)
    c: Coincident(g56,g57)
    c: Coincident(g57,g58)
    c: Coincident(g58,g59)
    c: Coincident(g59,g47)
    c: Coincident(g60,g61)
    c: Coincident(g61,g62)
    c: Coincident(g62,g63)
    c: Coincident(g63,g64)
    c: Coincident(g64,g65)
    c: Coincident(g65,g66)
    c: Coincident(g66,g67)
    c: Coincident(g67,g68)
    c: Coincident(g68,g69)
    c: Coincident(g69,g70)
    c: Coincident(g70,g71)
    c: Coincident(g71,g60)
    c: Coincident(g72,g73)
    c: Coincident(g73,g74)
    c: Coincident(g74,g75)
    c: Coincident(g75,g76)
    c: Coincident(g76,g77)
    c: Coincident(g77,g78)
    c: Coincident(g78,g79)
    c: Coincident(g79,g80)
    c: Coincident(g80,g81)
    c: Coincident(g81,g82)
    c: Coincident(g82,g83)
    c: Coincident(g83,g84)
    c: Coincident(g84,g85)
    c: Coincident(g85,g86)
    c: Coincident(g86,g87)
    c: Coincident(g87,g88)
    c: Coincident(g88,g89)
    c: Coincident(g89,g72)
    c: Coincident(g90,g91)
    c: Coincident(g91,g92)
    c: Coincident(g92,g93)
    c: Coincident(g93,g90)
    c: Coincident(g94,g95)
    c: Coincident(g95,g96)
    c: Coincident(g96,g97)
    c: Coincident(g97,g98)
    c: Coincident(g98,g99)
    c: Coincident(g99,g100)
    c: Coincident(g100,g101)
    c: Coincident(g101,g94)
    c: Coincident(g102,g103)
    c: Coincident(g103,g104)
    c: Coincident(g104,g105)
    c: Coincident(g105,g106)
    c: Coincident(g106,g107)
    c: Coincident(g107,g108)
    c: Coincident(g108,g109)
    c: Coincident(g109,g102)
    c: Coincident(g110,g111)
    c: Coincident(g111,g112)
    c: Coincident(g112,g113)
    c: Coincident(g113,g114)
    c: Coincident(g114,g115)
    c: Coincident(g115,g116)
    c: Coincident(g116,g117)
    c: Coincident(g117,g118)
    c: Coincident(g118,g119)
    c: Coincident(g119,g120)
    c: Coincident(g120,g121)
    c: Coincident(g121,g122)
    c: Coincident(g122,g123)
    c: Coincident(g123,g124)
    c: Coincident(g124,g125)
    c: Coincident(g125,g126)
    c: Coincident(g126,g127)
    c: Coincident(g127,g128)
    c: Coincident(g128,g129)
    c: Coincident(g129,g130)
    c: Coincident(g130,g131)
    c: Coincident(g131,g132)
    c: Coincident(g132,g133)
    c: Coincident(g133,g134)
    c: Coincident(g134,g135)
    c: Coincident(g135,g136)
    c: Coincident(g136,g110)
    c: Coincident(g137,g138)
    c: Coincident(g138,g139)
    c: Coincident(g139,g140)
    c: Coincident(g140,g141)
    c: Coincident(g141,g142)
    c: Coincident(g142,g143)
    c: Coincident(g143,g144)
    c: Coincident(g144,g145)
    c: Coincident(g145,g146)
    c: Coincident(g146,g147)
    c: Coincident(g147,g148)
    c: Coincident(g148,g149)
    c: Coincident(g149,g137)
    c: Coincident(g150,g151)
    c: Coincident(g151,g152)
    c: Coincident(g152,g153)
    c: Coincident(g153,g154)
    c: Coincident(g154,g155)
    c: Coincident(g155,g156)
    c: Coincident(g156,g157)
    c: Coincident(g157,g158)
    c: Coincident(g158,g159)
    c: Coincident(g159,g160)
    c: Coincident(g160,g161)
    c: Coincident(g161,g150)
    c: Coincident(g162,g163)
    c: Coincident(g163,g164)
    c: Coincident(g164,g165)
    c: Coincident(g165,g166)
    c: Coincident(g166,g167)
    c: Coincident(g167,g168)
    c: Coincident(g168,g169)
    c: Coincident(g169,g170)
    c: Coincident(g170,g171)
    c: Coincident(g171,g172)
    c: Coincident(g172,g173)
    c: Coincident(g173,g174)
    c: Coincident(g174,g175)
    c: Coincident(g175,g176)
    c: Coincident(g176,g177)
    c: Coincident(g177,g178)
    c: Coincident(g178,g179)
    c: Coincident(g179,g162)
    c: Coincident(g180,g181)
    c: Coincident(g181,g182)
    c: Coincident(g182,g183)
    c: Coincident(g183,g180)
FEATURE [Part::FeaturePython] Sketch_On_Surface002  # WARN: FeaturePython — macro-defined, semantics opaque (R4)
  ConstructionBounds = true
  FillExtrusion = true
  FillFaces = true
  Placement = pos=(0,0,-3) rot=(0,0,1;0rad)
  ReverseU = false
  ReverseV = false
  Sketch = -> Mapped_Sketch002
  SwapUV = false
  Thickness = 20
FEATURE [Part::Cut] Cut015024  label="cilindros_cafe_exterior_letras"
  Base = -> Cut015022
  Tool = -> Sketch_On_Surface002
FEATURE [Part::Cut] Cut015025  label="taza_cafe_exterior2"
  Base = -> Cut015024
  Tool = -> Fusion004
FEATURE [App::DocumentObjectGroup] Group005  label="exterior001"
  Group = -> [Compound005,Sketch_On_Surface001,Compound005001,Sketch001,Cut015025]
FEATURE [App::DocumentObjectGroup] Group001  label="taza_cafe"
  Group = -> [Group005,Group006]
FEATURE [Mesh::Feature] Mesh  label="taza_cafe_interior_2 (Meshed)"
FEATURE [Mesh::Feature] Mesh001  label="taza_cafe_exterior2 (Meshed)"
FEATURE [Part::MultiFuse] Fusion005  label="cortador003"
  Shapes = -> [Box009,Box007,Box006]
FEATURE [Part::Box] Box012  label="Cube012"
  AttacherType = Attacher::AttachEngine3D
  Height = 16.5
  Length = 30
  Placement = pos=(24,-7.65,2) rot=(0,0,1;0rad)
  Width = 15.3
FEATURE [Part::Box] Box013  label="Cube013"
  AttacherType = Attacher::AttachEngine3D
  Height = 25.5
  Length = 30
  Placement = pos=(24,-4.65,2) rot=(0,0,1;0rad)
  Width = 9.3
FEATURE [Part::Box] Box014  label="Cube014"
  AttacherType = Attacher::AttachEngine3D
  Height = 25.5
  Length = 30
  Placement = pos=(24,-0.5,-2) rot=(0,0,1;0rad)
  Width = 1
FEATURE [Part::MultiFuse] Fusion006  label="cortador004"
  Shapes = -> [Box014,Box013,Box012]
FEATURE [Part::Cut] Cut015026  label="taza_te_exterior2"
  Base = -> Cut015019
  Tool = -> Fusion005
FEATURE [App::DocumentObjectGroup] Group004  label="exterior"
  Group = -> [Compound004,Sketch,Cut015026]
FEATURE [Mesh::Feature] Mesh002  label="taza_te_exterior2 (Meshed)"
FEATURE [Part::Cut] Cut015027  label="taza_te_interior2"
  Base = -> Cut015014
  Tool = -> Fusion006
FEATURE [App::DocumentObjectGroup] Group003  label="interior"
  Group = -> [Cut015027]
FEATURE [App::DocumentObjectGroup] Group  label="taza_te"
  Group = -> [Group003,Group004]
FEATURE [Mesh::Feature] Mesh003  label="taza_te_interior2 (Meshed)"
